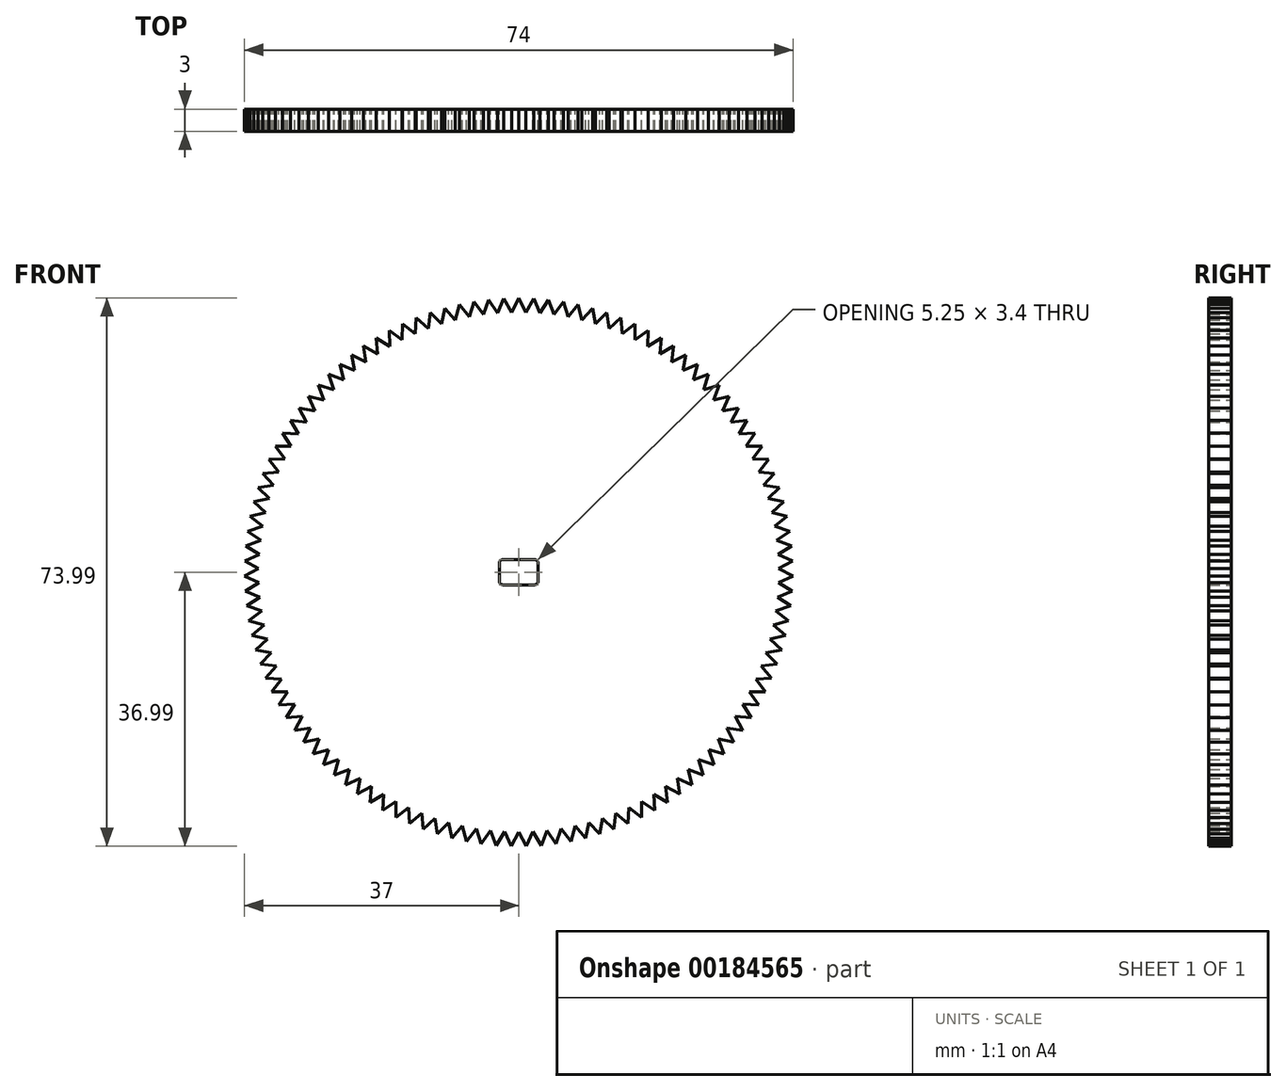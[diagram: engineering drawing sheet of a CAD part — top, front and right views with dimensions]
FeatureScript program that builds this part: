
annotation { "Feature Type Name" : "Feature", "Feature Type Description" : "" }
export const myFeature = defineFeature(function(context is Context, id is Id, definition is map)
    precondition{}
    {
        {
            var Q0;
            Q0=qCreatedBy(makeId("Front.planeOp"),FACE);
            var sketch = newSketch(context, id + "F0", { "sketchPlane" : qUnion([Q0])});
            skCircle(sketch, "E0", {"center": v(0, 0) * mm, "radius": 30 * mm});
            skSolve(sketch);
        }
        {
            var Q0;
            Q0=makeQuery(id+"F0.imprint","IMPRINT",FACE,{"disambiguationData":[TD([[makeQuery(id+"F0.imprint","IMPRINT",EDGE,{"derivedFrom":sQuery(id+"F0.wireOp",EDGE,"E0")}),1.0]])]});
            extrude(context, id + "F1", {"entities" : qUnion([Q0]), "depth" : 3 * mm});
        }
        {
            var Q0;
            Q0=makeQuery(id+"F1.opExtrude","CAP_FACE",FACE,{"disambiguationData":[OSD([sQuery(id+"F0.wireOp",EDGE,"E0")])],"isStart":false});
            var sketch = newSketch(context, id + "F2", { "sketchPlane" : qUnion([Q0])});
            skCircle(sketch, "E1", {"center": v(0, 0) * mm, "radius": 35 * mm});
            skLineSegment(sketch, "E2", {"start": v(-1, 34.99) * mm, "end": v(0, 37) * mm});
            skLineSegment(sketch, "E3", {"start": v(0, 37) * mm, "end": v(1, 34.99) * mm});
            skLineSegment(sketch, "E4.1.0", {"start": v(-2.02, 36.94) * mm, "end": v(-0.91, 34.99) * mm});
            skLineSegment(sketch, "E4.1.1", {"start": v(-2.9, 34.88) * mm, "end": v(-2.02, 36.94) * mm});
            skLineSegment(sketch, "E4.2.0", {"start": v(-4.04, 36.78) * mm, "end": v(-2.82, 34.89) * mm});
            skLineSegment(sketch, "E4.2.1", {"start": v(-4.8, 34.67) * mm, "end": v(-4.04, 36.78) * mm});
            skLineSegment(sketch, "E4.3.0", {"start": v(-6.04, 36.5) * mm, "end": v(-4.72, 34.68) * mm});
            skLineSegment(sketch, "E4.3.1", {"start": v(-6.7, 34.35) * mm, "end": v(-6.04, 36.5) * mm});
            skLineSegment(sketch, "E4.4.0", {"start": v(-8.02, 36.12) * mm, "end": v(-6.6, 34.37) * mm});
            skLineSegment(sketch, "E4.4.1", {"start": v(-8.56, 33.94) * mm, "end": v(-8.02, 36.12) * mm});
            skLineSegment(sketch, "E4.5.0", {"start": v(-9.98, 35.63) * mm, "end": v(-8.48, 33.96) * mm});
            skLineSegment(sketch, "E4.5.1", {"start": v(-10.4, 33.42) * mm, "end": v(-9.98, 35.63) * mm});
            skLineSegment(sketch, "E4.6.0", {"start": v(-11.91, 35.03) * mm, "end": v(-10.32, 33.44) * mm});
            skLineSegment(sketch, "E4.6.1", {"start": v(-12.21, 32.8) * mm, "end": v(-11.91, 35.03) * mm});
            skLineSegment(sketch, "E4.7.0", {"start": v(-13.8, 34.33) * mm, "end": v(-12.13, 32.83) * mm});
            skLineSegment(sketch, "E4.7.1", {"start": v(-13.98, 32.08) * mm, "end": v(-13.8, 34.33) * mm});
            skLineSegment(sketch, "E4.8.0", {"start": v(-15.66, 33.52) * mm, "end": v(-13.9, 32.12) * mm});
            skLineSegment(sketch, "E4.8.1", {"start": v(-15.72, 31.27) * mm, "end": v(-15.66, 33.52) * mm});
            skLineSegment(sketch, "E4.9.0", {"start": v(-17.47, 32.62) * mm, "end": v(-15.64, 31.31) * mm});
            skLineSegment(sketch, "E4.9.1", {"start": v(-17.4, 30.37) * mm, "end": v(-17.47, 32.62) * mm});
            skLineSegment(sketch, "E4.10.0", {"start": v(-19.22, 31.61) * mm, "end": v(-17.32, 30.41) * mm});
            skLineSegment(sketch, "E4.10.1", {"start": v(-19.03, 29.37) * mm, "end": v(-19.22, 31.61) * mm});
            skLineSegment(sketch, "E4.11.0", {"start": v(-20.92, 30.52) * mm, "end": v(-18.96, 29.42) * mm});
            skLineSegment(sketch, "E4.11.1", {"start": v(-20.6, 28.29) * mm, "end": v(-20.92, 30.52) * mm});
            skLineSegment(sketch, "E4.12.0", {"start": v(-22.56, 29.33) * mm, "end": v(-20.54, 28.34) * mm});
            skLineSegment(sketch, "E4.12.1", {"start": v(-22.12, 27.12) * mm, "end": v(-22.56, 29.33) * mm});
            skLineSegment(sketch, "E4.13.0", {"start": v(-24.13, 28.05) * mm, "end": v(-22.05, 27.18) * mm});
            skLineSegment(sketch, "E4.13.1", {"start": v(-23.57, 25.87) * mm, "end": v(-24.13, 28.05) * mm});
            skLineSegment(sketch, "E4.14.0", {"start": v(-25.62, 26.7) * mm, "end": v(-23.5, 25.93) * mm});
            skLineSegment(sketch, "E4.14.1", {"start": v(-24.95, 24.55) * mm, "end": v(-25.62, 26.7) * mm});
            skLineSegment(sketch, "E4.15.0", {"start": v(-27.04, 25.25) * mm, "end": v(-24.89, 24.61) * mm});
            skLineSegment(sketch, "E4.15.1", {"start": v(-26.25, 23.15) * mm, "end": v(-27.04, 25.25) * mm});
            skLineSegment(sketch, "E4.16.0", {"start": v(-28.38, 23.74) * mm, "end": v(-26.2, 23.21) * mm});
            skLineSegment(sketch, "E4.16.1", {"start": v(-27.48, 21.68) * mm, "end": v(-28.38, 23.74) * mm});
            skLineSegment(sketch, "E4.17.0", {"start": v(-29.63, 22.15) * mm, "end": v(-27.42, 21.75) * mm});
            skLineSegment(sketch, "E4.17.1", {"start": v(-28.62, 20.15) * mm, "end": v(-29.63, 22.15) * mm});
            skLineSegment(sketch, "E4.18.0", {"start": v(-30.8, 20.5) * mm, "end": v(-28.57, 20.22) * mm});
            skLineSegment(sketch, "E4.18.1", {"start": v(-29.68, 18.55) * mm, "end": v(-30.8, 20.5) * mm});
            skLineSegment(sketch, "E4.19.0", {"start": v(-31.87, 18.8) * mm, "end": v(-29.63, 18.63) * mm});
            skLineSegment(sketch, "E4.19.1", {"start": v(-30.65, 16.9) * mm, "end": v(-31.87, 18.8) * mm});
            skLineSegment(sketch, "E4.20.0", {"start": v(-32.85, 17.02) * mm, "end": v(-30.6, 16.98) * mm});
            skLineSegment(sketch, "E4.20.1", {"start": v(-31.52, 15.2) * mm, "end": v(-32.85, 17.02) * mm});
            skLineSegment(sketch, "E4.21.0", {"start": v(-33.73, 15.2) * mm, "end": v(-31.49, 15.29) * mm});
            skLineSegment(sketch, "E4.21.1", {"start": v(-32.3, 13.46) * mm, "end": v(-33.73, 15.2) * mm});
            skLineSegment(sketch, "E4.22.0", {"start": v(-34.51, 13.34) * mm, "end": v(-32.27, 13.54) * mm});
            skLineSegment(sketch, "E4.22.1", {"start": v(-33, 11.68) * mm, "end": v(-34.51, 13.34) * mm});
            skLineSegment(sketch, "E4.23.0", {"start": v(-35.19, 11.43) * mm, "end": v(-32.96, 11.76) * mm});
            skLineSegment(sketch, "E4.23.1", {"start": v(-33.58, 9.86) * mm, "end": v(-35.19, 11.43) * mm});
            skLineSegment(sketch, "E4.24.0", {"start": v(-35.76, 9.5) * mm, "end": v(-33.56, 9.94) * mm});
            skLineSegment(sketch, "E4.24.1", {"start": v(-34.07, 8.01) * mm, "end": v(-35.76, 9.5) * mm});
            skLineSegment(sketch, "E4.25.0", {"start": v(-36.23, 7.53) * mm, "end": v(-34.05, 8.1) * mm});
            skLineSegment(sketch, "E4.25.1", {"start": v(-34.46, 6.14) * mm, "end": v(-36.23, 7.53) * mm});
            skLineSegment(sketch, "E4.26.0", {"start": v(-36.58, 5.54) * mm, "end": v(-34.44, 6.23) * mm});
            skLineSegment(sketch, "E4.26.1", {"start": v(-34.74, 4.25) * mm, "end": v(-36.58, 5.54) * mm});
            skLineSegment(sketch, "E4.27.0", {"start": v(-36.83, 3.53) * mm, "end": v(-34.73, 4.34) * mm});
            skLineSegment(sketch, "E4.27.1", {"start": v(-34.92, 2.34) * mm, "end": v(-36.83, 3.53) * mm});
            skLineSegment(sketch, "E4.28.0", {"start": v(-36.97, 1.52) * mm, "end": v(-34.92, 2.43) * mm});
            skLineSegment(sketch, "E4.28.1", {"start": v(-35, 0.43) * mm, "end": v(-36.97, 1.52) * mm});
            skLineSegment(sketch, "E4.29.0", {"start": v(-37, -0.5) * mm, "end": v(-35, 0.52) * mm});
            skLineSegment(sketch, "E4.29.1", {"start": v(-34.97, -1.48) * mm, "end": v(-37, -0.5) * mm});
            skLineSegment(sketch, "E4.30.0", {"start": v(-36.91, -2.52) * mm, "end": v(-34.97, -1.39) * mm});
            skLineSegment(sketch, "E4.30.1", {"start": v(-34.84, -3.39) * mm, "end": v(-36.91, -2.52) * mm});
            skLineSegment(sketch, "E4.31.0", {"start": v(-36.72, -4.54) * mm, "end": v(-34.84, -3.3) * mm});
            skLineSegment(sketch, "E4.31.1", {"start": v(-34.6, -5.28) * mm, "end": v(-36.72, -4.54) * mm});
            skLineSegment(sketch, "E4.32.0", {"start": v(-36.42, -6.54) * mm, "end": v(-34.61, -5.2) * mm});
            skLineSegment(sketch, "E4.32.1", {"start": v(-34.26, -7.16) * mm, "end": v(-36.42, -6.54) * mm});
            skLineSegment(sketch, "E4.33.0", {"start": v(-36, -8.51) * mm, "end": v(-34.28, -7.08) * mm});
            skLineSegment(sketch, "E4.33.1", {"start": v(-33.82, -9.02) * mm, "end": v(-36, -8.51) * mm});
            skLineSegment(sketch, "E4.34.0", {"start": v(-35.49, -10.47) * mm, "end": v(-33.84, -8.94) * mm});
            skLineSegment(sketch, "E4.34.1", {"start": v(-33.27, -10.86) * mm, "end": v(-35.49, -10.47) * mm});
            skLineSegment(sketch, "E4.35.0", {"start": v(-34.86, -12.4) * mm, "end": v(-33.3, -10.77) * mm});
            skLineSegment(sketch, "E4.35.1", {"start": v(-32.63, -12.66) * mm, "end": v(-34.86, -12.4) * mm});
            skLineSegment(sketch, "E4.36.0", {"start": v(-34.13, -14.28) * mm, "end": v(-32.66, -12.58) * mm});
            skLineSegment(sketch, "E4.36.1", {"start": v(-31.9, -14.42) * mm, "end": v(-34.13, -14.28) * mm});
            skLineSegment(sketch, "E4.37.0", {"start": v(-33.3, -16.12) * mm, "end": v(-31.93, -14.34) * mm});
            skLineSegment(sketch, "E4.37.1", {"start": v(-31.06, -16.14) * mm, "end": v(-33.3, -16.12) * mm});
            skLineSegment(sketch, "E4.38.0", {"start": v(-32.37, -17.91) * mm, "end": v(-31.1, -16.06) * mm});
            skLineSegment(sketch, "E4.38.1", {"start": v(-30.13, -17.81) * mm, "end": v(-32.37, -17.91) * mm});
            skLineSegment(sketch, "E4.39.0", {"start": v(-31.35, -19.65) * mm, "end": v(-30.17, -17.74) * mm});
            skLineSegment(sketch, "E4.39.1", {"start": v(-29.11, -19.43) * mm, "end": v(-31.35, -19.65) * mm});
            skLineSegment(sketch, "E4.40.0", {"start": v(-30.23, -21.34) * mm, "end": v(-29.16, -19.36) * mm});
            skLineSegment(sketch, "E4.40.1", {"start": v(-28, -21) * mm, "end": v(-30.23, -21.34) * mm});
            skLineSegment(sketch, "E4.41.0", {"start": v(-29.02, -22.96) * mm, "end": v(-28.06, -20.92) * mm});
            skLineSegment(sketch, "E4.41.1", {"start": v(-26.82, -22.5) * mm, "end": v(-29.02, -22.96) * mm});
            skLineSegment(sketch, "E4.42.0", {"start": v(-27.72, -24.5) * mm, "end": v(-26.87, -22.42) * mm});
            skLineSegment(sketch, "E4.42.1", {"start": v(-25.55, -23.92) * mm, "end": v(-27.72, -24.5) * mm});
            skLineSegment(sketch, "E4.43.0", {"start": v(-26.34, -25.98) * mm, "end": v(-25.6, -23.86) * mm});
            skLineSegment(sketch, "E4.43.1", {"start": v(-24.2, -25.28) * mm, "end": v(-26.34, -25.98) * mm});
            skLineSegment(sketch, "E4.44.0", {"start": v(-24.88, -27.38) * mm, "end": v(-24.27, -25.22) * mm});
            skLineSegment(sketch, "E4.44.1", {"start": v(-22.79, -26.57) * mm, "end": v(-24.88, -27.38) * mm});
            skLineSegment(sketch, "E4.45.0", {"start": v(-23.35, -28.7) * mm, "end": v(-22.85, -26.5) * mm});
            skLineSegment(sketch, "E4.45.1", {"start": v(-21.3, -27.77) * mm, "end": v(-23.35, -28.7) * mm});
            skLineSegment(sketch, "E4.46.0", {"start": v(-21.75, -29.93) * mm, "end": v(-21.37, -27.72) * mm});
            skLineSegment(sketch, "E4.46.1", {"start": v(-19.76, -28.9) * mm, "end": v(-21.75, -29.93) * mm});
            skLineSegment(sketch, "E4.47.0", {"start": v(-20.08, -31.08) * mm, "end": v(-19.83, -28.84) * mm});
            skLineSegment(sketch, "E4.47.1", {"start": v(-18.15, -29.93) * mm, "end": v(-20.08, -31.08) * mm});
            skLineSegment(sketch, "E4.48.0", {"start": v(-18.35, -32.13) * mm, "end": v(-18.22, -29.88) * mm});
            skLineSegment(sketch, "E4.48.1", {"start": v(-16.49, -30.87) * mm, "end": v(-18.35, -32.13) * mm});
            skLineSegment(sketch, "E4.49.0", {"start": v(-16.57, -33.08) * mm, "end": v(-16.56, -30.83) * mm});
            skLineSegment(sketch, "E4.49.1", {"start": v(-14.78, -31.73) * mm, "end": v(-16.57, -33.08) * mm});
            skLineSegment(sketch, "E4.50.0", {"start": v(-14.74, -33.94) * mm, "end": v(-14.86, -31.7) * mm});
            skLineSegment(sketch, "E4.50.1", {"start": v(-13.02, -32.49) * mm, "end": v(-14.74, -33.94) * mm});
            skLineSegment(sketch, "E4.51.0", {"start": v(-12.87, -34.7) * mm, "end": v(-13.1, -32.45) * mm});
            skLineSegment(sketch, "E4.51.1", {"start": v(-11.23, -33.15) * mm, "end": v(-12.87, -34.7) * mm});
            skLineSegment(sketch, "E4.52.0", {"start": v(-10.95, -35.34) * mm, "end": v(-11.31, -33.12) * mm});
            skLineSegment(sketch, "E4.52.1", {"start": v(-9.4, -33.71) * mm, "end": v(-10.95, -35.34) * mm});
            skLineSegment(sketch, "E4.53.0", {"start": v(-9, -35.89) * mm, "end": v(-9.49, -33.7) * mm});
            skLineSegment(sketch, "E4.53.1", {"start": v(-7.55, -34.18) * mm, "end": v(-9, -35.89) * mm});
            skLineSegment(sketch, "E4.54.0", {"start": v(-7.03, -36.33) * mm, "end": v(-7.63, -34.16) * mm});
            skLineSegment(sketch, "E4.54.1", {"start": v(-5.67, -34.54) * mm, "end": v(-7.03, -36.33) * mm});
            skLineSegment(sketch, "E4.55.0", {"start": v(-5.04, -36.66) * mm, "end": v(-5.75, -34.52) * mm});
            skLineSegment(sketch, "E4.55.1", {"start": v(-3.77, -34.8) * mm, "end": v(-5.04, -36.66) * mm});
            skLineSegment(sketch, "E4.56.0", {"start": v(-3.03, -36.88) * mm, "end": v(-3.86, -34.79) * mm});
            skLineSegment(sketch, "E4.56.1", {"start": v(-1.87, -34.95) * mm, "end": v(-3.03, -36.88) * mm});
            skLineSegment(sketch, "E4.57.0", {"start": v(-1.01, -36.99) * mm, "end": v(-1.96, -34.95) * mm});
            skLineSegment(sketch, "E4.57.1", {"start": v(0.04, -35) * mm, "end": v(-1.01, -36.99) * mm});
            skLineSegment(sketch, "E4.58.0", {"start": v(1.01, -36.99) * mm, "end": v(-0.04, -35) * mm});
            skLineSegment(sketch, "E4.58.1", {"start": v(1.96, -34.95) * mm, "end": v(1.01, -36.99) * mm});
            skLineSegment(sketch, "E4.59.0", {"start": v(3.03, -36.88) * mm, "end": v(1.87, -34.95) * mm});
            skLineSegment(sketch, "E4.59.1", {"start": v(3.86, -34.79) * mm, "end": v(3.03, -36.88) * mm});
            skLineSegment(sketch, "E4.60.0", {"start": v(5.04, -36.66) * mm, "end": v(3.77, -34.8) * mm});
            skLineSegment(sketch, "E4.60.1", {"start": v(5.75, -34.52) * mm, "end": v(5.04, -36.66) * mm});
            skLineSegment(sketch, "E4.61.0", {"start": v(7.03, -36.33) * mm, "end": v(5.67, -34.54) * mm});
            skLineSegment(sketch, "E4.61.1", {"start": v(7.63, -34.16) * mm, "end": v(7.03, -36.33) * mm});
            skLineSegment(sketch, "E4.62.0", {"start": v(9, -35.89) * mm, "end": v(7.55, -34.18) * mm});
            skLineSegment(sketch, "E4.62.1", {"start": v(9.49, -33.7) * mm, "end": v(9, -35.89) * mm});
            skLineSegment(sketch, "E4.63.0", {"start": v(10.95, -35.34) * mm, "end": v(9.4, -33.71) * mm});
            skLineSegment(sketch, "E4.63.1", {"start": v(11.31, -33.12) * mm, "end": v(10.95, -35.34) * mm});
            skLineSegment(sketch, "E4.64.0", {"start": v(12.87, -34.7) * mm, "end": v(11.23, -33.15) * mm});
            skLineSegment(sketch, "E4.64.1", {"start": v(13.1, -32.45) * mm, "end": v(12.87, -34.7) * mm});
            skLineSegment(sketch, "E4.65.0", {"start": v(14.74, -33.94) * mm, "end": v(13.02, -32.49) * mm});
            skLineSegment(sketch, "E4.65.1", {"start": v(14.86, -31.7) * mm, "end": v(14.74, -33.94) * mm});
            skLineSegment(sketch, "E4.66.0", {"start": v(16.57, -33.08) * mm, "end": v(14.78, -31.73) * mm});
            skLineSegment(sketch, "E4.66.1", {"start": v(16.56, -30.83) * mm, "end": v(16.57, -33.08) * mm});
            skLineSegment(sketch, "E4.67.0", {"start": v(18.35, -32.13) * mm, "end": v(16.49, -30.87) * mm});
            skLineSegment(sketch, "E4.67.1", {"start": v(18.22, -29.88) * mm, "end": v(18.35, -32.13) * mm});
            skLineSegment(sketch, "E4.68.0", {"start": v(20.08, -31.08) * mm, "end": v(18.15, -29.93) * mm});
            skLineSegment(sketch, "E4.68.1", {"start": v(19.83, -28.84) * mm, "end": v(20.08, -31.08) * mm});
            skLineSegment(sketch, "E4.69.0", {"start": v(21.75, -29.93) * mm, "end": v(19.76, -28.9) * mm});
            skLineSegment(sketch, "E4.69.1", {"start": v(21.37, -27.72) * mm, "end": v(21.75, -29.93) * mm});
            skLineSegment(sketch, "E4.70.0", {"start": v(23.35, -28.7) * mm, "end": v(21.3, -27.77) * mm});
            skLineSegment(sketch, "E4.70.1", {"start": v(22.85, -26.5) * mm, "end": v(23.35, -28.7) * mm});
            skLineSegment(sketch, "E4.71.0", {"start": v(24.88, -27.38) * mm, "end": v(22.79, -26.57) * mm});
            skLineSegment(sketch, "E4.71.1", {"start": v(24.27, -25.22) * mm, "end": v(24.88, -27.38) * mm});
            skLineSegment(sketch, "E4.72.0", {"start": v(26.34, -25.98) * mm, "end": v(24.2, -25.28) * mm});
            skLineSegment(sketch, "E4.72.1", {"start": v(25.6, -23.86) * mm, "end": v(26.34, -25.98) * mm});
            skLineSegment(sketch, "E4.73.0", {"start": v(27.72, -24.5) * mm, "end": v(25.55, -23.92) * mm});
            skLineSegment(sketch, "E4.73.1", {"start": v(26.87, -22.42) * mm, "end": v(27.72, -24.5) * mm});
            skLineSegment(sketch, "E4.74.0", {"start": v(29.02, -22.96) * mm, "end": v(26.82, -22.5) * mm});
            skLineSegment(sketch, "E4.74.1", {"start": v(28.06, -20.92) * mm, "end": v(29.02, -22.96) * mm});
            skLineSegment(sketch, "E4.75.0", {"start": v(30.23, -21.34) * mm, "end": v(28, -21) * mm});
            skLineSegment(sketch, "E4.75.1", {"start": v(29.16, -19.36) * mm, "end": v(30.23, -21.34) * mm});
            skLineSegment(sketch, "E4.76.0", {"start": v(31.35, -19.65) * mm, "end": v(29.11, -19.43) * mm});
            skLineSegment(sketch, "E4.76.1", {"start": v(30.17, -17.74) * mm, "end": v(31.35, -19.65) * mm});
            skLineSegment(sketch, "E4.77.0", {"start": v(32.37, -17.91) * mm, "end": v(30.13, -17.81) * mm});
            skLineSegment(sketch, "E4.77.1", {"start": v(31.1, -16.06) * mm, "end": v(32.37, -17.91) * mm});
            skLineSegment(sketch, "E4.78.0", {"start": v(33.3, -16.12) * mm, "end": v(31.06, -16.14) * mm});
            skLineSegment(sketch, "E4.78.1", {"start": v(31.93, -14.34) * mm, "end": v(33.3, -16.12) * mm});
            skLineSegment(sketch, "E4.79.0", {"start": v(34.13, -14.28) * mm, "end": v(31.9, -14.42) * mm});
            skLineSegment(sketch, "E4.79.1", {"start": v(32.66, -12.58) * mm, "end": v(34.13, -14.28) * mm});
            skLineSegment(sketch, "E4.80.0", {"start": v(34.86, -12.4) * mm, "end": v(32.63, -12.66) * mm});
            skLineSegment(sketch, "E4.80.1", {"start": v(33.3, -10.77) * mm, "end": v(34.86, -12.4) * mm});
            skLineSegment(sketch, "E4.81.0", {"start": v(35.49, -10.47) * mm, "end": v(33.27, -10.86) * mm});
            skLineSegment(sketch, "E4.81.1", {"start": v(33.84, -8.94) * mm, "end": v(35.49, -10.47) * mm});
            skLineSegment(sketch, "E4.82.0", {"start": v(36, -8.51) * mm, "end": v(33.82, -9.02) * mm});
            skLineSegment(sketch, "E4.82.1", {"start": v(34.28, -7.08) * mm, "end": v(36, -8.51) * mm});
            skLineSegment(sketch, "E4.83.0", {"start": v(36.42, -6.54) * mm, "end": v(34.26, -7.16) * mm});
            skLineSegment(sketch, "E4.83.1", {"start": v(34.61, -5.2) * mm, "end": v(36.42, -6.54) * mm});
            skLineSegment(sketch, "E4.84.0", {"start": v(36.72, -4.54) * mm, "end": v(34.6, -5.28) * mm});
            skLineSegment(sketch, "E4.84.1", {"start": v(34.84, -3.3) * mm, "end": v(36.72, -4.54) * mm});
            skLineSegment(sketch, "E5.2.85.0", {"start": v(36.91, -2.52) * mm, "end": v(34.84, -3.39) * mm});
            skLineSegment(sketch, "E5.3.85.0", {"start": v(34.97, -1.39) * mm, "end": v(36.91, -2.52) * mm});
            skLineSegment(sketch, "E5.2.86.0", {"start": v(37, -0.5) * mm, "end": v(34.97, -1.48) * mm});
            skLineSegment(sketch, "E5.3.86.0", {"start": v(35, 0.52) * mm, "end": v(37, -0.5) * mm});
            skLineSegment(sketch, "E5.2.87.0", {"start": v(36.97, 1.52) * mm, "end": v(35, 0.43) * mm});
            skLineSegment(sketch, "E5.3.87.0", {"start": v(34.92, 2.43) * mm, "end": v(36.97, 1.52) * mm});
            skLineSegment(sketch, "E5.2.88.0", {"start": v(36.83, 3.53) * mm, "end": v(34.92, 2.34) * mm});
            skLineSegment(sketch, "E5.3.88.0", {"start": v(34.73, 4.34) * mm, "end": v(36.83, 3.53) * mm});
            skLineSegment(sketch, "E5.2.89.0", {"start": v(36.58, 5.54) * mm, "end": v(34.74, 4.25) * mm});
            skLineSegment(sketch, "E5.3.89.0", {"start": v(34.44, 6.23) * mm, "end": v(36.58, 5.54) * mm});
            skLineSegment(sketch, "E5.2.90.0", {"start": v(36.23, 7.53) * mm, "end": v(34.46, 6.14) * mm});
            skLineSegment(sketch, "E5.3.90.0", {"start": v(34.05, 8.1) * mm, "end": v(36.23, 7.53) * mm});
            skLineSegment(sketch, "E5.2.91.0", {"start": v(35.76, 9.5) * mm, "end": v(34.07, 8.01) * mm});
            skLineSegment(sketch, "E5.3.91.0", {"start": v(33.56, 9.94) * mm, "end": v(35.76, 9.5) * mm});
            skLineSegment(sketch, "E5.2.92.0", {"start": v(35.19, 11.43) * mm, "end": v(33.58, 9.86) * mm});
            skLineSegment(sketch, "E5.3.92.0", {"start": v(32.96, 11.76) * mm, "end": v(35.19, 11.43) * mm});
            skLineSegment(sketch, "E5.2.93.0", {"start": v(34.51, 13.34) * mm, "end": v(33, 11.68) * mm});
            skLineSegment(sketch, "E5.3.93.0", {"start": v(32.27, 13.54) * mm, "end": v(34.51, 13.34) * mm});
            skLineSegment(sketch, "E5.2.94.0", {"start": v(33.73, 15.2) * mm, "end": v(32.3, 13.46) * mm});
            skLineSegment(sketch, "E5.3.94.0", {"start": v(31.49, 15.29) * mm, "end": v(33.73, 15.2) * mm});
            skLineSegment(sketch, "E5.2.95.0", {"start": v(32.85, 17.02) * mm, "end": v(31.52, 15.2) * mm});
            skLineSegment(sketch, "E5.3.95.0", {"start": v(30.6, 16.98) * mm, "end": v(32.85, 17.02) * mm});
            skLineSegment(sketch, "E5.2.96.0", {"start": v(31.87, 18.8) * mm, "end": v(30.65, 16.9) * mm});
            skLineSegment(sketch, "E5.3.96.0", {"start": v(29.63, 18.63) * mm, "end": v(31.87, 18.8) * mm});
            skLineSegment(sketch, "E5.2.97.0", {"start": v(30.8, 20.5) * mm, "end": v(29.68, 18.55) * mm});
            skLineSegment(sketch, "E5.3.97.0", {"start": v(28.57, 20.22) * mm, "end": v(30.8, 20.5) * mm});
            skLineSegment(sketch, "E5.2.98.0", {"start": v(29.63, 22.15) * mm, "end": v(28.62, 20.15) * mm});
            skLineSegment(sketch, "E5.3.98.0", {"start": v(27.42, 21.75) * mm, "end": v(29.63, 22.15) * mm});
            skLineSegment(sketch, "E5.2.99.0", {"start": v(28.38, 23.74) * mm, "end": v(27.48, 21.68) * mm});
            skLineSegment(sketch, "E5.3.99.0", {"start": v(26.2, 23.21) * mm, "end": v(28.38, 23.74) * mm});
            skLineSegment(sketch, "E6.2.100.0", {"start": v(27.04, 25.25) * mm, "end": v(26.25, 23.15) * mm});
            skLineSegment(sketch, "E6.3.100.0", {"start": v(24.89, 24.61) * mm, "end": v(27.04, 25.25) * mm});
            skLineSegment(sketch, "E6.2.101.0", {"start": v(25.62, 26.7) * mm, "end": v(24.95, 24.55) * mm});
            skLineSegment(sketch, "E6.3.101.0", {"start": v(23.5, 25.93) * mm, "end": v(25.62, 26.7) * mm});
            skLineSegment(sketch, "E6.2.102.0", {"start": v(24.13, 28.05) * mm, "end": v(23.57, 25.87) * mm});
            skLineSegment(sketch, "E6.3.102.0", {"start": v(22.05, 27.18) * mm, "end": v(24.13, 28.05) * mm});
            skLineSegment(sketch, "E6.2.103.0", {"start": v(22.56, 29.33) * mm, "end": v(22.12, 27.12) * mm});
            skLineSegment(sketch, "E6.3.103.0", {"start": v(20.54, 28.34) * mm, "end": v(22.56, 29.33) * mm});
            skLineSegment(sketch, "E6.2.104.0", {"start": v(20.92, 30.52) * mm, "end": v(20.6, 28.29) * mm});
            skLineSegment(sketch, "E6.3.104.0", {"start": v(18.96, 29.42) * mm, "end": v(20.92, 30.52) * mm});
            skLineSegment(sketch, "E6.2.105.0", {"start": v(19.22, 31.61) * mm, "end": v(19.03, 29.37) * mm});
            skLineSegment(sketch, "E6.3.105.0", {"start": v(17.32, 30.41) * mm, "end": v(19.22, 31.61) * mm});
            skLineSegment(sketch, "E6.2.106.0", {"start": v(17.47, 32.62) * mm, "end": v(17.4, 30.37) * mm});
            skLineSegment(sketch, "E6.3.106.0", {"start": v(15.64, 31.31) * mm, "end": v(17.47, 32.62) * mm});
            skLineSegment(sketch, "E6.2.107.0", {"start": v(15.66, 33.52) * mm, "end": v(15.72, 31.27) * mm});
            skLineSegment(sketch, "E6.3.107.0", {"start": v(13.9, 32.12) * mm, "end": v(15.66, 33.52) * mm});
            skLineSegment(sketch, "E6.2.108.0", {"start": v(13.8, 34.33) * mm, "end": v(13.98, 32.08) * mm});
            skLineSegment(sketch, "E6.3.108.0", {"start": v(12.13, 32.83) * mm, "end": v(13.8, 34.33) * mm});
            skLineSegment(sketch, "E6.2.109.0", {"start": v(11.91, 35.03) * mm, "end": v(12.21, 32.8) * mm});
            skLineSegment(sketch, "E6.3.109.0", {"start": v(10.32, 33.44) * mm, "end": v(11.91, 35.03) * mm});
            skLineSegment(sketch, "E6.2.110.0", {"start": v(9.98, 35.63) * mm, "end": v(10.4, 33.42) * mm});
            skLineSegment(sketch, "E6.3.110.0", {"start": v(8.48, 33.96) * mm, "end": v(9.98, 35.63) * mm});
            skLineSegment(sketch, "E6.2.111.0", {"start": v(8.02, 36.12) * mm, "end": v(8.56, 33.94) * mm});
            skLineSegment(sketch, "E6.3.111.0", {"start": v(6.6, 34.37) * mm, "end": v(8.02, 36.12) * mm});
            skLineSegment(sketch, "E6.2.112.0", {"start": v(6.04, 36.5) * mm, "end": v(6.7, 34.35) * mm});
            skLineSegment(sketch, "E6.3.112.0", {"start": v(4.72, 34.68) * mm, "end": v(6.04, 36.5) * mm});
            skLineSegment(sketch, "E6.2.113.0", {"start": v(4.04, 36.78) * mm, "end": v(4.8, 34.67) * mm});
            skLineSegment(sketch, "E6.3.113.0", {"start": v(2.82, 34.89) * mm, "end": v(4.04, 36.78) * mm});
            skLineSegment(sketch, "E6.2.114.0", {"start": v(2.02, 36.94) * mm, "end": v(2.9, 34.88) * mm});
            skLineSegment(sketch, "E6.3.114.0", {"start": v(0.91, 34.99) * mm, "end": v(2.02, 36.94) * mm});
            skSolve(sketch);
        }
        {
            var Q0;
            Q0=makeQuery(id+"F2.imprint","IMPRINT",FACE,{"disambiguationData":[TD([[makeQuery(id+"F2.imprint","IMPRINT",EDGE,{"derivedFrom":makeQuery(id+"F1.opExtrude","CAP_EDGE",EDGE,{"disambiguationData":[OSD([sQuery(id+"F0.wireOp",EDGE,"E0")])],"isStart":false})}),-1.0]])]});
            var Q1;
            {var subQ3=sQuery(id+"F2.wireOp",EDGE,"E4.8.1");var subQ5=sQuery(id+"F2.wireOp",EDGE,"E1");var subQ6=makeQuery(id+"F2.imprint","INTERSECT",VERTEX,{"derivedFrom":[subQ5,subQ3]});Q1=makeQuery(id+"F2.imprint","IMPRINT",FACE,{"disambiguationData":[TD([[makeQuery(id+"F2.imprint","IMPRINT",EDGE,{"disambiguationData":[TD([[subQ6,-1.0]])],"derivedFrom":subQ5}),-1.0]])]});}
            var Q2;
            {var subQ5=sQuery(id+"F2.wireOp",EDGE,"E4.7.1");var subQ7=sQuery(id+"F2.wireOp",EDGE,"E1");var subQ8=makeQuery(id+"F2.imprint","INTERSECT",VERTEX,{"derivedFrom":[subQ7,subQ5]});Q2=makeQuery(id+"F2.imprint","IMPRINT",FACE,{"disambiguationData":[TD([[makeQuery(id+"F2.imprint","IMPRINT",EDGE,{"disambiguationData":[TD([[subQ8,-1.0]])],"derivedFrom":subQ7}),-1.0]])]});}
            var Q3;
            {var subQ5=sQuery(id+"F2.wireOp",EDGE,"E4.6.1");var subQ7=sQuery(id+"F2.wireOp",EDGE,"E1");var subQ8=makeQuery(id+"F2.imprint","INTERSECT",VERTEX,{"derivedFrom":[subQ7,subQ5]});Q3=makeQuery(id+"F2.imprint","IMPRINT",FACE,{"disambiguationData":[TD([[makeQuery(id+"F2.imprint","IMPRINT",EDGE,{"disambiguationData":[TD([[subQ8,-1.0]])],"derivedFrom":subQ7}),-1.0]])]});}
            var Q4;
            {var subQ5=sQuery(id+"F2.wireOp",EDGE,"E4.5.1");var subQ6=sQuery(id+"F2.wireOp",EDGE,"E1");var subQ7=makeQuery(id+"F2.imprint","INTERSECT",VERTEX,{"derivedFrom":[subQ6,subQ5]});Q4=makeQuery(id+"F2.imprint","IMPRINT",FACE,{"disambiguationData":[TD([[makeQuery(id+"F2.imprint","IMPRINT",EDGE,{"disambiguationData":[TD([[subQ7,-1.0]])],"derivedFrom":subQ6}),-1.0]])]});}
            var Q5;
            {var subQ3=sQuery(id+"F2.wireOp",EDGE,"E4.4.1");var subQ5=sQuery(id+"F2.wireOp",EDGE,"E1");var subQ6=makeQuery(id+"F2.imprint","INTERSECT",VERTEX,{"derivedFrom":[subQ5,subQ3]});Q5=makeQuery(id+"F2.imprint","IMPRINT",FACE,{"disambiguationData":[TD([[makeQuery(id+"F2.imprint","IMPRINT",EDGE,{"disambiguationData":[TD([[subQ6,-1.0]])],"derivedFrom":subQ5}),-1.0]])]});}
            var Q6;
            {var subQ5=sQuery(id+"F2.wireOp",EDGE,"E4.3.1");var subQ7=sQuery(id+"F2.wireOp",EDGE,"E1");var subQ8=makeQuery(id+"F2.imprint","INTERSECT",VERTEX,{"derivedFrom":[subQ7,subQ5]});Q6=makeQuery(id+"F2.imprint","IMPRINT",FACE,{"disambiguationData":[TD([[makeQuery(id+"F2.imprint","IMPRINT",EDGE,{"disambiguationData":[TD([[subQ8,-1.0]])],"derivedFrom":subQ7}),-1.0]])]});}
            var Q7;
            {var subQ5=sQuery(id+"F2.wireOp",EDGE,"E4.2.1");var subQ7=sQuery(id+"F2.wireOp",EDGE,"E1");var subQ8=makeQuery(id+"F2.imprint","INTERSECT",VERTEX,{"derivedFrom":[subQ7,subQ5]});Q7=makeQuery(id+"F2.imprint","IMPRINT",FACE,{"disambiguationData":[TD([[makeQuery(id+"F2.imprint","IMPRINT",EDGE,{"disambiguationData":[TD([[subQ8,-1.0]])],"derivedFrom":subQ7}),-1.0]])]});}
            var Q8;
            {var subQ3=sQuery(id+"F2.wireOp",EDGE,"E4.1.1");var subQ7=sQuery(id+"F2.wireOp",EDGE,"E1");var subQ8=makeQuery(id+"F2.imprint","INTERSECT",VERTEX,{"derivedFrom":[subQ7,subQ3]});Q8=makeQuery(id+"F2.imprint","IMPRINT",FACE,{"disambiguationData":[TD([[makeQuery(id+"F2.imprint","IMPRINT",EDGE,{"disambiguationData":[TD([[subQ8,-1.0]])],"derivedFrom":subQ7}),-1.0]])]});}
            var Q9;
            {var subQ5=sQuery(id+"F2.wireOp",EDGE,"E2");var subQ7=sQuery(id+"F2.wireOp",EDGE,"E1");var subQ8=makeQuery(id+"F2.imprint","INTERSECT",VERTEX,{"derivedFrom":[subQ7,subQ5]});Q9=makeQuery(id+"F2.imprint","IMPRINT",FACE,{"disambiguationData":[TD([[makeQuery(id+"F2.imprint","IMPRINT",EDGE,{"disambiguationData":[TD([[subQ8,-1.0]])],"derivedFrom":subQ7}),-1.0]])]});}
            var Q10;
            {var subQ0=sQuery(id+"F2.wireOp",EDGE,"E4.1.0");var subQ1=sQuery(id+"F2.wireOp",EDGE,"E1");var subQ2=makeQuery(id+"F2.imprint","INTERSECT",VERTEX,{"derivedFrom":[subQ1,subQ0]});Q10=makeQuery(id+"F2.imprint","IMPRINT",FACE,{"disambiguationData":[TD([[makeQuery(id+"F2.imprint","IMPRINT",EDGE,{"disambiguationData":[TD([[subQ2,1.0]])],"derivedFrom":subQ1}),-1.0]])]});}
            var Q11;
            {var subQ5=sQuery(id+"F2.wireOp",EDGE,"E1");var subQ7=sQuery(id+"F2.wireOp",EDGE,"E3");var subQ8=makeQuery(id+"F2.imprint","INTERSECT",VERTEX,{"derivedFrom":[subQ5,subQ7]});Q11=makeQuery(id+"F2.imprint","IMPRINT",FACE,{"disambiguationData":[TD([[makeQuery(id+"F2.imprint","IMPRINT",EDGE,{"disambiguationData":[TD([[subQ8,1.0]])],"derivedFrom":subQ5}),-1.0]])]});}
            var Q12;
            {var subQ0=sQuery(id+"F2.wireOp",EDGE,"E5.3.86.0");var subQ1=sQuery(id+"F2.wireOp",EDGE,"E1");var subQ2=makeQuery(id+"F2.imprint","INTERSECT",VERTEX,{"derivedFrom":[subQ1,subQ0]});Q12=makeQuery(id+"F2.imprint","IMPRINT",FACE,{"disambiguationData":[TD([[makeQuery(id+"F2.imprint","IMPRINT",EDGE,{"disambiguationData":[TD([[subQ2,1.0]])],"derivedFrom":subQ1}),-1.0]])]});}
            var Q13;
            {var subQ0=sQuery(id+"F2.wireOp",EDGE,"E5.3.87.0");var subQ1=sQuery(id+"F2.wireOp",EDGE,"E1");var subQ2=makeQuery(id+"F2.imprint","INTERSECT",VERTEX,{"derivedFrom":[subQ1,subQ0]});Q13=makeQuery(id+"F2.imprint","IMPRINT",FACE,{"disambiguationData":[TD([[makeQuery(id+"F2.imprint","IMPRINT",EDGE,{"disambiguationData":[TD([[subQ2,1.0]])],"derivedFrom":subQ1}),-1.0]])]});}
            var Q14;
            {var subQ0=sQuery(id+"F2.wireOp",EDGE,"E5.3.88.0");var subQ1=sQuery(id+"F2.wireOp",EDGE,"E1");var subQ2=makeQuery(id+"F2.imprint","INTERSECT",VERTEX,{"derivedFrom":[subQ1,subQ0]});Q14=makeQuery(id+"F2.imprint","IMPRINT",FACE,{"disambiguationData":[TD([[makeQuery(id+"F2.imprint","IMPRINT",EDGE,{"disambiguationData":[TD([[subQ2,1.0]])],"derivedFrom":subQ1}),-1.0]])]});}
            var Q15;
            {var subQ0=sQuery(id+"F2.wireOp",EDGE,"E5.3.89.0");var subQ1=sQuery(id+"F2.wireOp",EDGE,"E1");var subQ2=makeQuery(id+"F2.imprint","INTERSECT",VERTEX,{"derivedFrom":[subQ1,subQ0]});Q15=makeQuery(id+"F2.imprint","IMPRINT",FACE,{"disambiguationData":[TD([[makeQuery(id+"F2.imprint","IMPRINT",EDGE,{"disambiguationData":[TD([[subQ2,1.0]])],"derivedFrom":subQ1}),-1.0]])]});}
            var Q16;
            {var subQ0=sQuery(id+"F2.wireOp",EDGE,"E5.3.90.0");var subQ1=sQuery(id+"F2.wireOp",EDGE,"E1");var subQ2=makeQuery(id+"F2.imprint","INTERSECT",VERTEX,{"derivedFrom":[subQ1,subQ0]});Q16=makeQuery(id+"F2.imprint","IMPRINT",FACE,{"disambiguationData":[TD([[makeQuery(id+"F2.imprint","IMPRINT",EDGE,{"disambiguationData":[TD([[subQ2,1.0]])],"derivedFrom":subQ1}),-1.0]])]});}
            var Q17;
            {var subQ0=sQuery(id+"F2.wireOp",EDGE,"E5.3.91.0");var subQ1=sQuery(id+"F2.wireOp",EDGE,"E1");var subQ2=makeQuery(id+"F2.imprint","INTERSECT",VERTEX,{"derivedFrom":[subQ1,subQ0]});Q17=makeQuery(id+"F2.imprint","IMPRINT",FACE,{"disambiguationData":[TD([[makeQuery(id+"F2.imprint","IMPRINT",EDGE,{"disambiguationData":[TD([[subQ2,1.0]])],"derivedFrom":subQ1}),-1.0]])]});}
            var Q18;
            {var subQ0=sQuery(id+"F2.wireOp",EDGE,"E5.3.92.0");var subQ1=sQuery(id+"F2.wireOp",EDGE,"E1");var subQ2=makeQuery(id+"F2.imprint","INTERSECT",VERTEX,{"derivedFrom":[subQ1,subQ0]});Q18=makeQuery(id+"F2.imprint","IMPRINT",FACE,{"disambiguationData":[TD([[makeQuery(id+"F2.imprint","IMPRINT",EDGE,{"disambiguationData":[TD([[subQ2,1.0]])],"derivedFrom":subQ1}),-1.0]])]});}
            var Q19;
            {var subQ0=sQuery(id+"F2.wireOp",EDGE,"E5.3.93.0");var subQ1=sQuery(id+"F2.wireOp",EDGE,"E1");var subQ2=makeQuery(id+"F2.imprint","INTERSECT",VERTEX,{"derivedFrom":[subQ1,subQ0]});Q19=makeQuery(id+"F2.imprint","IMPRINT",FACE,{"disambiguationData":[TD([[makeQuery(id+"F2.imprint","IMPRINT",EDGE,{"disambiguationData":[TD([[subQ2,1.0]])],"derivedFrom":subQ1}),-1.0]])]});}
            var Q20;
            {var subQ0=sQuery(id+"F2.wireOp",EDGE,"E5.3.94.0");var subQ1=sQuery(id+"F2.wireOp",EDGE,"E1");var subQ2=makeQuery(id+"F2.imprint","INTERSECT",VERTEX,{"derivedFrom":[subQ1,subQ0]});Q20=makeQuery(id+"F2.imprint","IMPRINT",FACE,{"disambiguationData":[TD([[makeQuery(id+"F2.imprint","IMPRINT",EDGE,{"disambiguationData":[TD([[subQ2,1.0]])],"derivedFrom":subQ1}),-1.0]])]});}
            var Q21;
            {var subQ0=sQuery(id+"F2.wireOp",EDGE,"E5.3.95.0");var subQ1=sQuery(id+"F2.wireOp",EDGE,"E1");var subQ2=makeQuery(id+"F2.imprint","INTERSECT",VERTEX,{"derivedFrom":[subQ1,subQ0]});Q21=makeQuery(id+"F2.imprint","IMPRINT",FACE,{"disambiguationData":[TD([[makeQuery(id+"F2.imprint","IMPRINT",EDGE,{"disambiguationData":[TD([[subQ2,1.0]])],"derivedFrom":subQ1}),-1.0]])]});}
            var Q22;
            {var subQ0=sQuery(id+"F2.wireOp",EDGE,"E5.3.96.0");var subQ1=sQuery(id+"F2.wireOp",EDGE,"E1");var subQ2=makeQuery(id+"F2.imprint","INTERSECT",VERTEX,{"derivedFrom":[subQ1,subQ0]});Q22=makeQuery(id+"F2.imprint","IMPRINT",FACE,{"disambiguationData":[TD([[makeQuery(id+"F2.imprint","IMPRINT",EDGE,{"disambiguationData":[TD([[subQ2,1.0]])],"derivedFrom":subQ1}),-1.0]])]});}
            var Q23;
            {var subQ0=sQuery(id+"F2.wireOp",EDGE,"E5.3.97.0");var subQ1=sQuery(id+"F2.wireOp",EDGE,"E1");var subQ2=makeQuery(id+"F2.imprint","INTERSECT",VERTEX,{"derivedFrom":[subQ1,subQ0]});Q23=makeQuery(id+"F2.imprint","IMPRINT",FACE,{"disambiguationData":[TD([[makeQuery(id+"F2.imprint","IMPRINT",EDGE,{"disambiguationData":[TD([[subQ2,1.0]])],"derivedFrom":subQ1}),-1.0]])]});}
            var Q24;
            {var subQ0=sQuery(id+"F2.wireOp",EDGE,"E5.3.98.0");var subQ1=sQuery(id+"F2.wireOp",EDGE,"E1");var subQ2=makeQuery(id+"F2.imprint","INTERSECT",VERTEX,{"derivedFrom":[subQ1,subQ0]});Q24=makeQuery(id+"F2.imprint","IMPRINT",FACE,{"disambiguationData":[TD([[makeQuery(id+"F2.imprint","IMPRINT",EDGE,{"disambiguationData":[TD([[subQ2,1.0]])],"derivedFrom":subQ1}),-1.0]])]});}
            var Q25;
            {var subQ0=sQuery(id+"F2.wireOp",EDGE,"E5.3.99.0");var subQ1=sQuery(id+"F2.wireOp",EDGE,"E1");var subQ2=makeQuery(id+"F2.imprint","INTERSECT",VERTEX,{"derivedFrom":[subQ1,subQ0]});Q25=makeQuery(id+"F2.imprint","IMPRINT",FACE,{"disambiguationData":[TD([[makeQuery(id+"F2.imprint","IMPRINT",EDGE,{"disambiguationData":[TD([[subQ2,1.0]])],"derivedFrom":subQ1}),-1.0]])]});}
            var Q26;
            {var subQ0=sQuery(id+"F2.wireOp",EDGE,"E6.3.100.0");var subQ1=sQuery(id+"F2.wireOp",EDGE,"E1");var subQ2=makeQuery(id+"F2.imprint","INTERSECT",VERTEX,{"derivedFrom":[subQ1,subQ0]});Q26=makeQuery(id+"F2.imprint","IMPRINT",FACE,{"disambiguationData":[TD([[makeQuery(id+"F2.imprint","IMPRINT",EDGE,{"disambiguationData":[TD([[subQ2,1.0]])],"derivedFrom":subQ1}),-1.0]])]});}
            var Q27;
            {var subQ0=sQuery(id+"F2.wireOp",EDGE,"E6.3.101.0");var subQ1=sQuery(id+"F2.wireOp",EDGE,"E1");var subQ2=makeQuery(id+"F2.imprint","INTERSECT",VERTEX,{"derivedFrom":[subQ1,subQ0]});Q27=makeQuery(id+"F2.imprint","IMPRINT",FACE,{"disambiguationData":[TD([[makeQuery(id+"F2.imprint","IMPRINT",EDGE,{"disambiguationData":[TD([[subQ2,1.0]])],"derivedFrom":subQ1}),-1.0]])]});}
            var Q28;
            {var subQ0=sQuery(id+"F2.wireOp",EDGE,"E6.3.102.0");var subQ1=sQuery(id+"F2.wireOp",EDGE,"E1");var subQ2=makeQuery(id+"F2.imprint","INTERSECT",VERTEX,{"derivedFrom":[subQ1,subQ0]});Q28=makeQuery(id+"F2.imprint","IMPRINT",FACE,{"disambiguationData":[TD([[makeQuery(id+"F2.imprint","IMPRINT",EDGE,{"disambiguationData":[TD([[subQ2,1.0]])],"derivedFrom":subQ1}),-1.0]])]});}
            var Q29;
            {var subQ0=sQuery(id+"F2.wireOp",EDGE,"E6.3.103.0");var subQ1=sQuery(id+"F2.wireOp",EDGE,"E1");var subQ2=makeQuery(id+"F2.imprint","INTERSECT",VERTEX,{"derivedFrom":[subQ1,subQ0]});Q29=makeQuery(id+"F2.imprint","IMPRINT",FACE,{"disambiguationData":[TD([[makeQuery(id+"F2.imprint","IMPRINT",EDGE,{"disambiguationData":[TD([[subQ2,1.0]])],"derivedFrom":subQ1}),-1.0]])]});}
            var Q30;
            {var subQ0=sQuery(id+"F2.wireOp",EDGE,"E6.3.104.0");var subQ1=sQuery(id+"F2.wireOp",EDGE,"E1");var subQ2=makeQuery(id+"F2.imprint","INTERSECT",VERTEX,{"derivedFrom":[subQ1,subQ0]});Q30=makeQuery(id+"F2.imprint","IMPRINT",FACE,{"disambiguationData":[TD([[makeQuery(id+"F2.imprint","IMPRINT",EDGE,{"disambiguationData":[TD([[subQ2,1.0]])],"derivedFrom":subQ1}),-1.0]])]});}
            var Q31;
            {var subQ0=sQuery(id+"F2.wireOp",EDGE,"E6.3.105.0");var subQ1=sQuery(id+"F2.wireOp",EDGE,"E1");var subQ2=makeQuery(id+"F2.imprint","INTERSECT",VERTEX,{"derivedFrom":[subQ1,subQ0]});Q31=makeQuery(id+"F2.imprint","IMPRINT",FACE,{"disambiguationData":[TD([[makeQuery(id+"F2.imprint","IMPRINT",EDGE,{"disambiguationData":[TD([[subQ2,1.0]])],"derivedFrom":subQ1}),-1.0]])]});}
            var Q32;
            {var subQ0=sQuery(id+"F2.wireOp",EDGE,"E6.3.106.0");var subQ1=sQuery(id+"F2.wireOp",EDGE,"E1");var subQ2=makeQuery(id+"F2.imprint","INTERSECT",VERTEX,{"derivedFrom":[subQ1,subQ0]});Q32=makeQuery(id+"F2.imprint","IMPRINT",FACE,{"disambiguationData":[TD([[makeQuery(id+"F2.imprint","IMPRINT",EDGE,{"disambiguationData":[TD([[subQ2,1.0]])],"derivedFrom":subQ1}),-1.0]])]});}
            var Q33;
            {var subQ0=sQuery(id+"F2.wireOp",EDGE,"E6.3.107.0");var subQ1=sQuery(id+"F2.wireOp",EDGE,"E1");var subQ2=makeQuery(id+"F2.imprint","INTERSECT",VERTEX,{"derivedFrom":[subQ1,subQ0]});Q33=makeQuery(id+"F2.imprint","IMPRINT",FACE,{"disambiguationData":[TD([[makeQuery(id+"F2.imprint","IMPRINT",EDGE,{"disambiguationData":[TD([[subQ2,1.0]])],"derivedFrom":subQ1}),-1.0]])]});}
            var Q34;
            {var subQ0=sQuery(id+"F2.wireOp",EDGE,"E6.3.108.0");var subQ1=sQuery(id+"F2.wireOp",EDGE,"E1");var subQ2=makeQuery(id+"F2.imprint","INTERSECT",VERTEX,{"derivedFrom":[subQ1,subQ0]});Q34=makeQuery(id+"F2.imprint","IMPRINT",FACE,{"disambiguationData":[TD([[makeQuery(id+"F2.imprint","IMPRINT",EDGE,{"disambiguationData":[TD([[subQ2,1.0]])],"derivedFrom":subQ1}),-1.0]])]});}
            var Q35;
            {var subQ0=sQuery(id+"F2.wireOp",EDGE,"E6.3.109.0");var subQ1=sQuery(id+"F2.wireOp",EDGE,"E1");var subQ2=makeQuery(id+"F2.imprint","INTERSECT",VERTEX,{"derivedFrom":[subQ1,subQ0]});Q35=makeQuery(id+"F2.imprint","IMPRINT",FACE,{"disambiguationData":[TD([[makeQuery(id+"F2.imprint","IMPRINT",EDGE,{"disambiguationData":[TD([[subQ2,1.0]])],"derivedFrom":subQ1}),-1.0]])]});}
            var Q36;
            {var subQ0=sQuery(id+"F2.wireOp",EDGE,"E6.3.110.0");var subQ1=sQuery(id+"F2.wireOp",EDGE,"E1");var subQ2=makeQuery(id+"F2.imprint","INTERSECT",VERTEX,{"derivedFrom":[subQ1,subQ0]});Q36=makeQuery(id+"F2.imprint","IMPRINT",FACE,{"disambiguationData":[TD([[makeQuery(id+"F2.imprint","IMPRINT",EDGE,{"disambiguationData":[TD([[subQ2,1.0]])],"derivedFrom":subQ1}),-1.0]])]});}
            var Q37;
            {var subQ0=sQuery(id+"F2.wireOp",EDGE,"E6.3.111.0");var subQ1=sQuery(id+"F2.wireOp",EDGE,"E1");var subQ2=makeQuery(id+"F2.imprint","INTERSECT",VERTEX,{"derivedFrom":[subQ1,subQ0]});Q37=makeQuery(id+"F2.imprint","IMPRINT",FACE,{"disambiguationData":[TD([[makeQuery(id+"F2.imprint","IMPRINT",EDGE,{"disambiguationData":[TD([[subQ2,1.0]])],"derivedFrom":subQ1}),-1.0]])]});}
            var Q38;
            {var subQ0=sQuery(id+"F2.wireOp",EDGE,"E6.3.112.0");var subQ1=sQuery(id+"F2.wireOp",EDGE,"E1");var subQ2=makeQuery(id+"F2.imprint","INTERSECT",VERTEX,{"derivedFrom":[subQ1,subQ0]});Q38=makeQuery(id+"F2.imprint","IMPRINT",FACE,{"disambiguationData":[TD([[makeQuery(id+"F2.imprint","IMPRINT",EDGE,{"disambiguationData":[TD([[subQ2,1.0]])],"derivedFrom":subQ1}),-1.0]])]});}
            var Q39;
            {var subQ0=sQuery(id+"F2.wireOp",EDGE,"E6.3.113.0");var subQ1=sQuery(id+"F2.wireOp",EDGE,"E1");var subQ2=makeQuery(id+"F2.imprint","INTERSECT",VERTEX,{"derivedFrom":[subQ1,subQ0]});Q39=makeQuery(id+"F2.imprint","IMPRINT",FACE,{"disambiguationData":[TD([[makeQuery(id+"F2.imprint","IMPRINT",EDGE,{"disambiguationData":[TD([[subQ2,1.0]])],"derivedFrom":subQ1}),-1.0]])]});}
            var Q40;
            {var subQ0=sQuery(id+"F2.wireOp",EDGE,"E3");var subQ1=sQuery(id+"F2.wireOp",EDGE,"E1");var subQ2=makeQuery(id+"F2.imprint","INTERSECT",VERTEX,{"derivedFrom":[subQ1,subQ0]});Q40=makeQuery(id+"F2.imprint","IMPRINT",FACE,{"disambiguationData":[TD([[makeQuery(id+"F2.imprint","IMPRINT",EDGE,{"disambiguationData":[TD([[subQ2,-1.0]])],"derivedFrom":subQ1}),-1.0]])]});}
            var Q41;
            {var subQ0=sQuery(id+"F2.wireOp",EDGE,"E2");var subQ1=sQuery(id+"F2.wireOp",EDGE,"E1");var subQ2=makeQuery(id+"F2.imprint","INTERSECT",VERTEX,{"derivedFrom":[subQ1,subQ0]});Q41=makeQuery(id+"F2.imprint","IMPRINT",FACE,{"disambiguationData":[TD([[makeQuery(id+"F2.imprint","IMPRINT",EDGE,{"disambiguationData":[TD([[subQ2,1.0]])],"derivedFrom":subQ1}),-1.0]])]});}
            var Q42;
            {var subQ0=sQuery(id+"F2.wireOp",EDGE,"E4.1.1");var subQ1=sQuery(id+"F2.wireOp",EDGE,"E1");var subQ2=makeQuery(id+"F2.imprint","INTERSECT",VERTEX,{"derivedFrom":[subQ1,subQ0]});Q42=makeQuery(id+"F2.imprint","IMPRINT",FACE,{"disambiguationData":[TD([[makeQuery(id+"F2.imprint","IMPRINT",EDGE,{"disambiguationData":[TD([[subQ2,1.0]])],"derivedFrom":subQ1}),-1.0]])]});}
            var Q43;
            {var subQ0=sQuery(id+"F2.wireOp",EDGE,"E4.2.1");var subQ1=sQuery(id+"F2.wireOp",EDGE,"E1");var subQ2=makeQuery(id+"F2.imprint","INTERSECT",VERTEX,{"derivedFrom":[subQ1,subQ0]});Q43=makeQuery(id+"F2.imprint","IMPRINT",FACE,{"disambiguationData":[TD([[makeQuery(id+"F2.imprint","IMPRINT",EDGE,{"disambiguationData":[TD([[subQ2,1.0]])],"derivedFrom":subQ1}),-1.0]])]});}
            var Q44;
            {var subQ0=sQuery(id+"F2.wireOp",EDGE,"E4.3.1");var subQ1=sQuery(id+"F2.wireOp",EDGE,"E1");var subQ2=makeQuery(id+"F2.imprint","INTERSECT",VERTEX,{"derivedFrom":[subQ1,subQ0]});Q44=makeQuery(id+"F2.imprint","IMPRINT",FACE,{"disambiguationData":[TD([[makeQuery(id+"F2.imprint","IMPRINT",EDGE,{"disambiguationData":[TD([[subQ2,1.0]])],"derivedFrom":subQ1}),-1.0]])]});}
            var Q45;
            {var subQ0=sQuery(id+"F2.wireOp",EDGE,"E4.4.1");var subQ1=sQuery(id+"F2.wireOp",EDGE,"E1");var subQ2=makeQuery(id+"F2.imprint","INTERSECT",VERTEX,{"derivedFrom":[subQ1,subQ0]});Q45=makeQuery(id+"F2.imprint","IMPRINT",FACE,{"disambiguationData":[TD([[makeQuery(id+"F2.imprint","IMPRINT",EDGE,{"disambiguationData":[TD([[subQ2,1.0]])],"derivedFrom":subQ1}),-1.0]])]});}
            var Q46;
            {var subQ0=sQuery(id+"F2.wireOp",EDGE,"E4.5.1");var subQ1=sQuery(id+"F2.wireOp",EDGE,"E1");var subQ2=makeQuery(id+"F2.imprint","INTERSECT",VERTEX,{"derivedFrom":[subQ1,subQ0]});Q46=makeQuery(id+"F2.imprint","IMPRINT",FACE,{"disambiguationData":[TD([[makeQuery(id+"F2.imprint","IMPRINT",EDGE,{"disambiguationData":[TD([[subQ2,1.0]])],"derivedFrom":subQ1}),-1.0]])]});}
            var Q47;
            {var subQ0=sQuery(id+"F2.wireOp",EDGE,"E4.6.1");var subQ1=sQuery(id+"F2.wireOp",EDGE,"E1");var subQ2=makeQuery(id+"F2.imprint","INTERSECT",VERTEX,{"derivedFrom":[subQ1,subQ0]});Q47=makeQuery(id+"F2.imprint","IMPRINT",FACE,{"disambiguationData":[TD([[makeQuery(id+"F2.imprint","IMPRINT",EDGE,{"disambiguationData":[TD([[subQ2,1.0]])],"derivedFrom":subQ1}),-1.0]])]});}
            var Q48;
            {var subQ0=sQuery(id+"F2.wireOp",EDGE,"E4.7.1");var subQ1=sQuery(id+"F2.wireOp",EDGE,"E1");var subQ2=makeQuery(id+"F2.imprint","INTERSECT",VERTEX,{"derivedFrom":[subQ1,subQ0]});Q48=makeQuery(id+"F2.imprint","IMPRINT",FACE,{"disambiguationData":[TD([[makeQuery(id+"F2.imprint","IMPRINT",EDGE,{"disambiguationData":[TD([[subQ2,1.0]])],"derivedFrom":subQ1}),-1.0]])]});}
            var Q49;
            {var subQ0=sQuery(id+"F2.wireOp",EDGE,"E4.8.1");var subQ1=sQuery(id+"F2.wireOp",EDGE,"E1");var subQ2=makeQuery(id+"F2.imprint","INTERSECT",VERTEX,{"derivedFrom":[subQ1,subQ0]});Q49=makeQuery(id+"F2.imprint","IMPRINT",FACE,{"disambiguationData":[TD([[makeQuery(id+"F2.imprint","IMPRINT",EDGE,{"disambiguationData":[TD([[subQ2,1.0]])],"derivedFrom":subQ1}),-1.0]])]});}
            var Q50;
            {var subQ0=sQuery(id+"F2.wireOp",EDGE,"E4.9.1");var subQ1=sQuery(id+"F2.wireOp",EDGE,"E1");var subQ2=makeQuery(id+"F2.imprint","INTERSECT",VERTEX,{"derivedFrom":[subQ1,subQ0]});Q50=makeQuery(id+"F2.imprint","IMPRINT",FACE,{"disambiguationData":[TD([[makeQuery(id+"F2.imprint","IMPRINT",EDGE,{"disambiguationData":[TD([[subQ2,1.0]])],"derivedFrom":subQ1}),-1.0]])]});}
            var Q51;
            {var subQ0=sQuery(id+"F2.wireOp",EDGE,"E4.10.1");var subQ1=sQuery(id+"F2.wireOp",EDGE,"E1");var subQ2=makeQuery(id+"F2.imprint","INTERSECT",VERTEX,{"derivedFrom":[subQ1,subQ0]});Q51=makeQuery(id+"F2.imprint","IMPRINT",FACE,{"disambiguationData":[TD([[makeQuery(id+"F2.imprint","IMPRINT",EDGE,{"disambiguationData":[TD([[subQ2,1.0]])],"derivedFrom":subQ1}),-1.0]])]});}
            var Q52;
            {var subQ0=sQuery(id+"F2.wireOp",EDGE,"E4.11.1");var subQ1=sQuery(id+"F2.wireOp",EDGE,"E1");var subQ2=makeQuery(id+"F2.imprint","INTERSECT",VERTEX,{"derivedFrom":[subQ1,subQ0]});Q52=makeQuery(id+"F2.imprint","IMPRINT",FACE,{"disambiguationData":[TD([[makeQuery(id+"F2.imprint","IMPRINT",EDGE,{"disambiguationData":[TD([[subQ2,1.0]])],"derivedFrom":subQ1}),-1.0]])]});}
            var Q53;
            {var subQ0=sQuery(id+"F2.wireOp",EDGE,"E4.12.1");var subQ1=sQuery(id+"F2.wireOp",EDGE,"E1");var subQ2=makeQuery(id+"F2.imprint","INTERSECT",VERTEX,{"derivedFrom":[subQ1,subQ0]});Q53=makeQuery(id+"F2.imprint","IMPRINT",FACE,{"disambiguationData":[TD([[makeQuery(id+"F2.imprint","IMPRINT",EDGE,{"disambiguationData":[TD([[subQ2,1.0]])],"derivedFrom":subQ1}),-1.0]])]});}
            var Q54;
            {var subQ0=sQuery(id+"F2.wireOp",EDGE,"E4.13.1");var subQ1=sQuery(id+"F2.wireOp",EDGE,"E1");var subQ2=makeQuery(id+"F2.imprint","INTERSECT",VERTEX,{"derivedFrom":[subQ1,subQ0]});Q54=makeQuery(id+"F2.imprint","IMPRINT",FACE,{"disambiguationData":[TD([[makeQuery(id+"F2.imprint","IMPRINT",EDGE,{"disambiguationData":[TD([[subQ2,1.0]])],"derivedFrom":subQ1}),-1.0]])]});}
            var Q55;
            {var subQ0=sQuery(id+"F2.wireOp",EDGE,"E4.14.1");var subQ1=sQuery(id+"F2.wireOp",EDGE,"E1");var subQ2=makeQuery(id+"F2.imprint","INTERSECT",VERTEX,{"derivedFrom":[subQ1,subQ0]});Q55=makeQuery(id+"F2.imprint","IMPRINT",FACE,{"disambiguationData":[TD([[makeQuery(id+"F2.imprint","IMPRINT",EDGE,{"disambiguationData":[TD([[subQ2,1.0]])],"derivedFrom":subQ1}),-1.0]])]});}
            var Q56;
            {var subQ0=sQuery(id+"F2.wireOp",EDGE,"E4.15.1");var subQ1=sQuery(id+"F2.wireOp",EDGE,"E1");var subQ2=makeQuery(id+"F2.imprint","INTERSECT",VERTEX,{"derivedFrom":[subQ1,subQ0]});Q56=makeQuery(id+"F2.imprint","IMPRINT",FACE,{"disambiguationData":[TD([[makeQuery(id+"F2.imprint","IMPRINT",EDGE,{"disambiguationData":[TD([[subQ2,1.0]])],"derivedFrom":subQ1}),-1.0]])]});}
            var Q57;
            {var subQ0=sQuery(id+"F2.wireOp",EDGE,"E4.16.1");var subQ1=sQuery(id+"F2.wireOp",EDGE,"E1");var subQ2=makeQuery(id+"F2.imprint","INTERSECT",VERTEX,{"derivedFrom":[subQ1,subQ0]});Q57=makeQuery(id+"F2.imprint","IMPRINT",FACE,{"disambiguationData":[TD([[makeQuery(id+"F2.imprint","IMPRINT",EDGE,{"disambiguationData":[TD([[subQ2,1.0]])],"derivedFrom":subQ1}),-1.0]])]});}
            var Q58;
            {var subQ0=sQuery(id+"F2.wireOp",EDGE,"E4.17.1");var subQ1=sQuery(id+"F2.wireOp",EDGE,"E1");var subQ2=makeQuery(id+"F2.imprint","INTERSECT",VERTEX,{"derivedFrom":[subQ1,subQ0]});Q58=makeQuery(id+"F2.imprint","IMPRINT",FACE,{"disambiguationData":[TD([[makeQuery(id+"F2.imprint","IMPRINT",EDGE,{"disambiguationData":[TD([[subQ2,1.0]])],"derivedFrom":subQ1}),-1.0]])]});}
            var Q59;
            {var subQ0=sQuery(id+"F2.wireOp",EDGE,"E4.18.1");var subQ1=sQuery(id+"F2.wireOp",EDGE,"E1");var subQ2=makeQuery(id+"F2.imprint","INTERSECT",VERTEX,{"derivedFrom":[subQ1,subQ0]});Q59=makeQuery(id+"F2.imprint","IMPRINT",FACE,{"disambiguationData":[TD([[makeQuery(id+"F2.imprint","IMPRINT",EDGE,{"disambiguationData":[TD([[subQ2,1.0]])],"derivedFrom":subQ1}),-1.0]])]});}
            var Q60;
            {var subQ0=sQuery(id+"F2.wireOp",EDGE,"E4.19.1");var subQ1=sQuery(id+"F2.wireOp",EDGE,"E1");var subQ2=makeQuery(id+"F2.imprint","INTERSECT",VERTEX,{"derivedFrom":[subQ1,subQ0]});Q60=makeQuery(id+"F2.imprint","IMPRINT",FACE,{"disambiguationData":[TD([[makeQuery(id+"F2.imprint","IMPRINT",EDGE,{"disambiguationData":[TD([[subQ2,1.0]])],"derivedFrom":subQ1}),-1.0]])]});}
            var Q61;
            {var subQ0=sQuery(id+"F2.wireOp",EDGE,"E4.20.1");var subQ1=sQuery(id+"F2.wireOp",EDGE,"E1");var subQ2=makeQuery(id+"F2.imprint","INTERSECT",VERTEX,{"derivedFrom":[subQ1,subQ0]});Q61=makeQuery(id+"F2.imprint","IMPRINT",FACE,{"disambiguationData":[TD([[makeQuery(id+"F2.imprint","IMPRINT",EDGE,{"disambiguationData":[TD([[subQ2,1.0]])],"derivedFrom":subQ1}),-1.0]])]});}
            var Q62;
            {var subQ0=sQuery(id+"F2.wireOp",EDGE,"E4.21.1");var subQ1=sQuery(id+"F2.wireOp",EDGE,"E1");var subQ2=makeQuery(id+"F2.imprint","INTERSECT",VERTEX,{"derivedFrom":[subQ1,subQ0]});Q62=makeQuery(id+"F2.imprint","IMPRINT",FACE,{"disambiguationData":[TD([[makeQuery(id+"F2.imprint","IMPRINT",EDGE,{"disambiguationData":[TD([[subQ2,1.0]])],"derivedFrom":subQ1}),-1.0]])]});}
            var Q63;
            {var subQ0=sQuery(id+"F2.wireOp",EDGE,"E4.22.1");var subQ1=sQuery(id+"F2.wireOp",EDGE,"E1");var subQ2=makeQuery(id+"F2.imprint","INTERSECT",VERTEX,{"derivedFrom":[subQ1,subQ0]});Q63=makeQuery(id+"F2.imprint","IMPRINT",FACE,{"disambiguationData":[TD([[makeQuery(id+"F2.imprint","IMPRINT",EDGE,{"disambiguationData":[TD([[subQ2,1.0]])],"derivedFrom":subQ1}),-1.0]])]});}
            var Q64;
            {var subQ0=sQuery(id+"F2.wireOp",EDGE,"E4.23.1");var subQ1=sQuery(id+"F2.wireOp",EDGE,"E1");var subQ2=makeQuery(id+"F2.imprint","INTERSECT",VERTEX,{"derivedFrom":[subQ1,subQ0]});Q64=makeQuery(id+"F2.imprint","IMPRINT",FACE,{"disambiguationData":[TD([[makeQuery(id+"F2.imprint","IMPRINT",EDGE,{"disambiguationData":[TD([[subQ2,1.0]])],"derivedFrom":subQ1}),-1.0]])]});}
            var Q65;
            {var subQ0=sQuery(id+"F2.wireOp",EDGE,"E4.24.1");var subQ1=sQuery(id+"F2.wireOp",EDGE,"E1");var subQ2=makeQuery(id+"F2.imprint","INTERSECT",VERTEX,{"derivedFrom":[subQ1,subQ0]});Q65=makeQuery(id+"F2.imprint","IMPRINT",FACE,{"disambiguationData":[TD([[makeQuery(id+"F2.imprint","IMPRINT",EDGE,{"disambiguationData":[TD([[subQ2,1.0]])],"derivedFrom":subQ1}),-1.0]])]});}
            var Q66;
            {var subQ0=sQuery(id+"F2.wireOp",EDGE,"E4.25.1");var subQ1=sQuery(id+"F2.wireOp",EDGE,"E1");var subQ2=makeQuery(id+"F2.imprint","INTERSECT",VERTEX,{"derivedFrom":[subQ1,subQ0]});Q66=makeQuery(id+"F2.imprint","IMPRINT",FACE,{"disambiguationData":[TD([[makeQuery(id+"F2.imprint","IMPRINT",EDGE,{"disambiguationData":[TD([[subQ2,1.0]])],"derivedFrom":subQ1}),-1.0]])]});}
            var Q67;
            {var subQ0=sQuery(id+"F2.wireOp",EDGE,"E4.26.1");var subQ1=sQuery(id+"F2.wireOp",EDGE,"E1");var subQ2=makeQuery(id+"F2.imprint","INTERSECT",VERTEX,{"derivedFrom":[subQ1,subQ0]});Q67=makeQuery(id+"F2.imprint","IMPRINT",FACE,{"disambiguationData":[TD([[makeQuery(id+"F2.imprint","IMPRINT",EDGE,{"disambiguationData":[TD([[subQ2,1.0]])],"derivedFrom":subQ1}),-1.0]])]});}
            var Q68;
            {var subQ0=sQuery(id+"F2.wireOp",EDGE,"E4.27.1");var subQ1=sQuery(id+"F2.wireOp",EDGE,"E1");var subQ2=makeQuery(id+"F2.imprint","INTERSECT",VERTEX,{"derivedFrom":[subQ1,subQ0]});Q68=makeQuery(id+"F2.imprint","IMPRINT",FACE,{"disambiguationData":[TD([[makeQuery(id+"F2.imprint","IMPRINT",EDGE,{"disambiguationData":[TD([[subQ2,1.0]])],"derivedFrom":subQ1}),-1.0]])]});}
            var Q69;
            {var subQ0=sQuery(id+"F2.wireOp",EDGE,"E4.28.1");var subQ1=sQuery(id+"F2.wireOp",EDGE,"E1");var subQ2=makeQuery(id+"F2.imprint","INTERSECT",VERTEX,{"derivedFrom":[subQ1,subQ0]});Q69=makeQuery(id+"F2.imprint","IMPRINT",FACE,{"disambiguationData":[TD([[makeQuery(id+"F2.imprint","IMPRINT",EDGE,{"disambiguationData":[TD([[subQ2,1.0]])],"derivedFrom":subQ1}),-1.0]])]});}
            var Q70;
            {var subQ0=sQuery(id+"F2.wireOp",EDGE,"E4.29.1");var subQ1=sQuery(id+"F2.wireOp",EDGE,"E1");var subQ2=makeQuery(id+"F2.imprint","INTERSECT",VERTEX,{"derivedFrom":[subQ1,subQ0]});Q70=makeQuery(id+"F2.imprint","IMPRINT",FACE,{"disambiguationData":[TD([[makeQuery(id+"F2.imprint","IMPRINT",EDGE,{"disambiguationData":[TD([[subQ2,1.0]])],"derivedFrom":subQ1}),-1.0]])]});}
            var Q71;
            {var subQ0=sQuery(id+"F2.wireOp",EDGE,"E4.30.1");var subQ1=sQuery(id+"F2.wireOp",EDGE,"E1");var subQ2=makeQuery(id+"F2.imprint","INTERSECT",VERTEX,{"derivedFrom":[subQ1,subQ0]});Q71=makeQuery(id+"F2.imprint","IMPRINT",FACE,{"disambiguationData":[TD([[makeQuery(id+"F2.imprint","IMPRINT",EDGE,{"disambiguationData":[TD([[subQ2,1.0]])],"derivedFrom":subQ1}),-1.0]])]});}
            var Q72;
            {var subQ0=sQuery(id+"F2.wireOp",EDGE,"E4.31.1");var subQ1=sQuery(id+"F2.wireOp",EDGE,"E1");var subQ2=makeQuery(id+"F2.imprint","INTERSECT",VERTEX,{"derivedFrom":[subQ1,subQ0]});Q72=makeQuery(id+"F2.imprint","IMPRINT",FACE,{"disambiguationData":[TD([[makeQuery(id+"F2.imprint","IMPRINT",EDGE,{"disambiguationData":[TD([[subQ2,1.0]])],"derivedFrom":subQ1}),-1.0]])]});}
            var Q73;
            {var subQ0=sQuery(id+"F2.wireOp",EDGE,"E4.32.1");var subQ1=sQuery(id+"F2.wireOp",EDGE,"E1");var subQ2=makeQuery(id+"F2.imprint","INTERSECT",VERTEX,{"derivedFrom":[subQ1,subQ0]});Q73=makeQuery(id+"F2.imprint","IMPRINT",FACE,{"disambiguationData":[TD([[makeQuery(id+"F2.imprint","IMPRINT",EDGE,{"disambiguationData":[TD([[subQ2,1.0]])],"derivedFrom":subQ1}),-1.0]])]});}
            var Q74;
            {var subQ0=sQuery(id+"F2.wireOp",EDGE,"E4.33.1");var subQ1=sQuery(id+"F2.wireOp",EDGE,"E1");var subQ2=makeQuery(id+"F2.imprint","INTERSECT",VERTEX,{"derivedFrom":[subQ1,subQ0]});Q74=makeQuery(id+"F2.imprint","IMPRINT",FACE,{"disambiguationData":[TD([[makeQuery(id+"F2.imprint","IMPRINT",EDGE,{"disambiguationData":[TD([[subQ2,1.0]])],"derivedFrom":subQ1}),-1.0]])]});}
            var Q75;
            {var subQ0=sQuery(id+"F2.wireOp",EDGE,"E4.34.1");var subQ1=sQuery(id+"F2.wireOp",EDGE,"E1");var subQ2=makeQuery(id+"F2.imprint","INTERSECT",VERTEX,{"derivedFrom":[subQ1,subQ0]});Q75=makeQuery(id+"F2.imprint","IMPRINT",FACE,{"disambiguationData":[TD([[makeQuery(id+"F2.imprint","IMPRINT",EDGE,{"disambiguationData":[TD([[subQ2,1.0]])],"derivedFrom":subQ1}),-1.0]])]});}
            var Q76;
            {var subQ0=sQuery(id+"F2.wireOp",EDGE,"E4.35.1");var subQ1=sQuery(id+"F2.wireOp",EDGE,"E1");var subQ2=makeQuery(id+"F2.imprint","INTERSECT",VERTEX,{"derivedFrom":[subQ1,subQ0]});Q76=makeQuery(id+"F2.imprint","IMPRINT",FACE,{"disambiguationData":[TD([[makeQuery(id+"F2.imprint","IMPRINT",EDGE,{"disambiguationData":[TD([[subQ2,1.0]])],"derivedFrom":subQ1}),-1.0]])]});}
            var Q77;
            {var subQ0=sQuery(id+"F2.wireOp",EDGE,"E4.36.1");var subQ1=sQuery(id+"F2.wireOp",EDGE,"E1");var subQ2=makeQuery(id+"F2.imprint","INTERSECT",VERTEX,{"derivedFrom":[subQ1,subQ0]});Q77=makeQuery(id+"F2.imprint","IMPRINT",FACE,{"disambiguationData":[TD([[makeQuery(id+"F2.imprint","IMPRINT",EDGE,{"disambiguationData":[TD([[subQ2,1.0]])],"derivedFrom":subQ1}),-1.0]])]});}
            var Q78;
            {var subQ0=sQuery(id+"F2.wireOp",EDGE,"E4.37.1");var subQ1=sQuery(id+"F2.wireOp",EDGE,"E1");var subQ2=makeQuery(id+"F2.imprint","INTERSECT",VERTEX,{"derivedFrom":[subQ1,subQ0]});Q78=makeQuery(id+"F2.imprint","IMPRINT",FACE,{"disambiguationData":[TD([[makeQuery(id+"F2.imprint","IMPRINT",EDGE,{"disambiguationData":[TD([[subQ2,1.0]])],"derivedFrom":subQ1}),-1.0]])]});}
            var Q79;
            {var subQ0=sQuery(id+"F2.wireOp",EDGE,"E4.38.1");var subQ1=sQuery(id+"F2.wireOp",EDGE,"E1");var subQ2=makeQuery(id+"F2.imprint","INTERSECT",VERTEX,{"derivedFrom":[subQ1,subQ0]});Q79=makeQuery(id+"F2.imprint","IMPRINT",FACE,{"disambiguationData":[TD([[makeQuery(id+"F2.imprint","IMPRINT",EDGE,{"disambiguationData":[TD([[subQ2,1.0]])],"derivedFrom":subQ1}),-1.0]])]});}
            var Q80;
            {var subQ0=sQuery(id+"F2.wireOp",EDGE,"E4.39.1");var subQ1=sQuery(id+"F2.wireOp",EDGE,"E1");var subQ2=makeQuery(id+"F2.imprint","INTERSECT",VERTEX,{"derivedFrom":[subQ1,subQ0]});Q80=makeQuery(id+"F2.imprint","IMPRINT",FACE,{"disambiguationData":[TD([[makeQuery(id+"F2.imprint","IMPRINT",EDGE,{"disambiguationData":[TD([[subQ2,1.0]])],"derivedFrom":subQ1}),-1.0]])]});}
            var Q81;
            {var subQ0=sQuery(id+"F2.wireOp",EDGE,"E4.40.1");var subQ1=sQuery(id+"F2.wireOp",EDGE,"E1");var subQ2=makeQuery(id+"F2.imprint","INTERSECT",VERTEX,{"derivedFrom":[subQ1,subQ0]});Q81=makeQuery(id+"F2.imprint","IMPRINT",FACE,{"disambiguationData":[TD([[makeQuery(id+"F2.imprint","IMPRINT",EDGE,{"disambiguationData":[TD([[subQ2,1.0]])],"derivedFrom":subQ1}),-1.0]])]});}
            var Q82;
            {var subQ0=sQuery(id+"F2.wireOp",EDGE,"E4.41.1");var subQ1=sQuery(id+"F2.wireOp",EDGE,"E1");var subQ2=makeQuery(id+"F2.imprint","INTERSECT",VERTEX,{"derivedFrom":[subQ1,subQ0]});Q82=makeQuery(id+"F2.imprint","IMPRINT",FACE,{"disambiguationData":[TD([[makeQuery(id+"F2.imprint","IMPRINT",EDGE,{"disambiguationData":[TD([[subQ2,1.0]])],"derivedFrom":subQ1}),-1.0]])]});}
            var Q83;
            {var subQ0=sQuery(id+"F2.wireOp",EDGE,"E4.42.1");var subQ1=sQuery(id+"F2.wireOp",EDGE,"E1");var subQ2=makeQuery(id+"F2.imprint","INTERSECT",VERTEX,{"derivedFrom":[subQ1,subQ0]});Q83=makeQuery(id+"F2.imprint","IMPRINT",FACE,{"disambiguationData":[TD([[makeQuery(id+"F2.imprint","IMPRINT",EDGE,{"disambiguationData":[TD([[subQ2,1.0]])],"derivedFrom":subQ1}),-1.0]])]});}
            var Q84;
            {var subQ0=sQuery(id+"F2.wireOp",EDGE,"E4.43.1");var subQ1=sQuery(id+"F2.wireOp",EDGE,"E1");var subQ2=makeQuery(id+"F2.imprint","INTERSECT",VERTEX,{"derivedFrom":[subQ1,subQ0]});Q84=makeQuery(id+"F2.imprint","IMPRINT",FACE,{"disambiguationData":[TD([[makeQuery(id+"F2.imprint","IMPRINT",EDGE,{"disambiguationData":[TD([[subQ2,1.0]])],"derivedFrom":subQ1}),-1.0]])]});}
            var Q85;
            {var subQ0=sQuery(id+"F2.wireOp",EDGE,"E4.44.1");var subQ1=sQuery(id+"F2.wireOp",EDGE,"E1");var subQ2=makeQuery(id+"F2.imprint","INTERSECT",VERTEX,{"derivedFrom":[subQ1,subQ0]});Q85=makeQuery(id+"F2.imprint","IMPRINT",FACE,{"disambiguationData":[TD([[makeQuery(id+"F2.imprint","IMPRINT",EDGE,{"disambiguationData":[TD([[subQ2,1.0]])],"derivedFrom":subQ1}),-1.0]])]});}
            var Q86;
            {var subQ0=sQuery(id+"F2.wireOp",EDGE,"E4.45.1");var subQ1=sQuery(id+"F2.wireOp",EDGE,"E1");var subQ2=makeQuery(id+"F2.imprint","INTERSECT",VERTEX,{"derivedFrom":[subQ1,subQ0]});Q86=makeQuery(id+"F2.imprint","IMPRINT",FACE,{"disambiguationData":[TD([[makeQuery(id+"F2.imprint","IMPRINT",EDGE,{"disambiguationData":[TD([[subQ2,1.0]])],"derivedFrom":subQ1}),-1.0]])]});}
            var Q87;
            {var subQ0=sQuery(id+"F2.wireOp",EDGE,"E4.46.1");var subQ1=sQuery(id+"F2.wireOp",EDGE,"E1");var subQ2=makeQuery(id+"F2.imprint","INTERSECT",VERTEX,{"derivedFrom":[subQ1,subQ0]});Q87=makeQuery(id+"F2.imprint","IMPRINT",FACE,{"disambiguationData":[TD([[makeQuery(id+"F2.imprint","IMPRINT",EDGE,{"disambiguationData":[TD([[subQ2,1.0]])],"derivedFrom":subQ1}),-1.0]])]});}
            var Q88;
            {var subQ0=sQuery(id+"F2.wireOp",EDGE,"E4.47.1");var subQ1=sQuery(id+"F2.wireOp",EDGE,"E1");var subQ2=makeQuery(id+"F2.imprint","INTERSECT",VERTEX,{"derivedFrom":[subQ1,subQ0]});Q88=makeQuery(id+"F2.imprint","IMPRINT",FACE,{"disambiguationData":[TD([[makeQuery(id+"F2.imprint","IMPRINT",EDGE,{"disambiguationData":[TD([[subQ2,1.0]])],"derivedFrom":subQ1}),-1.0]])]});}
            var Q89;
            {var subQ0=sQuery(id+"F2.wireOp",EDGE,"E4.48.1");var subQ1=sQuery(id+"F2.wireOp",EDGE,"E1");var subQ2=makeQuery(id+"F2.imprint","INTERSECT",VERTEX,{"derivedFrom":[subQ1,subQ0]});Q89=makeQuery(id+"F2.imprint","IMPRINT",FACE,{"disambiguationData":[TD([[makeQuery(id+"F2.imprint","IMPRINT",EDGE,{"disambiguationData":[TD([[subQ2,1.0]])],"derivedFrom":subQ1}),-1.0]])]});}
            var Q90;
            {var subQ0=sQuery(id+"F2.wireOp",EDGE,"E4.49.1");var subQ1=sQuery(id+"F2.wireOp",EDGE,"E1");var subQ2=makeQuery(id+"F2.imprint","INTERSECT",VERTEX,{"derivedFrom":[subQ1,subQ0]});Q90=makeQuery(id+"F2.imprint","IMPRINT",FACE,{"disambiguationData":[TD([[makeQuery(id+"F2.imprint","IMPRINT",EDGE,{"disambiguationData":[TD([[subQ2,1.0]])],"derivedFrom":subQ1}),-1.0]])]});}
            var Q91;
            {var subQ0=sQuery(id+"F2.wireOp",EDGE,"E4.50.1");var subQ1=sQuery(id+"F2.wireOp",EDGE,"E1");var subQ2=makeQuery(id+"F2.imprint","INTERSECT",VERTEX,{"derivedFrom":[subQ1,subQ0]});Q91=makeQuery(id+"F2.imprint","IMPRINT",FACE,{"disambiguationData":[TD([[makeQuery(id+"F2.imprint","IMPRINT",EDGE,{"disambiguationData":[TD([[subQ2,1.0]])],"derivedFrom":subQ1}),-1.0]])]});}
            var Q92;
            {var subQ0=sQuery(id+"F2.wireOp",EDGE,"E4.51.1");var subQ1=sQuery(id+"F2.wireOp",EDGE,"E1");var subQ2=makeQuery(id+"F2.imprint","INTERSECT",VERTEX,{"derivedFrom":[subQ1,subQ0]});Q92=makeQuery(id+"F2.imprint","IMPRINT",FACE,{"disambiguationData":[TD([[makeQuery(id+"F2.imprint","IMPRINT",EDGE,{"disambiguationData":[TD([[subQ2,1.0]])],"derivedFrom":subQ1}),-1.0]])]});}
            var Q93;
            {var subQ0=sQuery(id+"F2.wireOp",EDGE,"E4.52.1");var subQ1=sQuery(id+"F2.wireOp",EDGE,"E1");var subQ2=makeQuery(id+"F2.imprint","INTERSECT",VERTEX,{"derivedFrom":[subQ1,subQ0]});Q93=makeQuery(id+"F2.imprint","IMPRINT",FACE,{"disambiguationData":[TD([[makeQuery(id+"F2.imprint","IMPRINT",EDGE,{"disambiguationData":[TD([[subQ2,1.0]])],"derivedFrom":subQ1}),-1.0]])]});}
            var Q94;
            {var subQ0=sQuery(id+"F2.wireOp",EDGE,"E4.53.1");var subQ1=sQuery(id+"F2.wireOp",EDGE,"E1");var subQ2=makeQuery(id+"F2.imprint","INTERSECT",VERTEX,{"derivedFrom":[subQ1,subQ0]});Q94=makeQuery(id+"F2.imprint","IMPRINT",FACE,{"disambiguationData":[TD([[makeQuery(id+"F2.imprint","IMPRINT",EDGE,{"disambiguationData":[TD([[subQ2,1.0]])],"derivedFrom":subQ1}),-1.0]])]});}
            var Q95;
            {var subQ0=sQuery(id+"F2.wireOp",EDGE,"E4.54.1");var subQ1=sQuery(id+"F2.wireOp",EDGE,"E1");var subQ2=makeQuery(id+"F2.imprint","INTERSECT",VERTEX,{"derivedFrom":[subQ1,subQ0]});Q95=makeQuery(id+"F2.imprint","IMPRINT",FACE,{"disambiguationData":[TD([[makeQuery(id+"F2.imprint","IMPRINT",EDGE,{"disambiguationData":[TD([[subQ2,1.0]])],"derivedFrom":subQ1}),-1.0]])]});}
            var Q96;
            {var subQ0=sQuery(id+"F2.wireOp",EDGE,"E4.55.1");var subQ1=sQuery(id+"F2.wireOp",EDGE,"E1");var subQ2=makeQuery(id+"F2.imprint","INTERSECT",VERTEX,{"derivedFrom":[subQ1,subQ0]});Q96=makeQuery(id+"F2.imprint","IMPRINT",FACE,{"disambiguationData":[TD([[makeQuery(id+"F2.imprint","IMPRINT",EDGE,{"disambiguationData":[TD([[subQ2,1.0]])],"derivedFrom":subQ1}),-1.0]])]});}
            var Q97;
            {var subQ0=sQuery(id+"F2.wireOp",EDGE,"E4.56.1");var subQ1=sQuery(id+"F2.wireOp",EDGE,"E1");var subQ2=makeQuery(id+"F2.imprint","INTERSECT",VERTEX,{"derivedFrom":[subQ1,subQ0]});Q97=makeQuery(id+"F2.imprint","IMPRINT",FACE,{"disambiguationData":[TD([[makeQuery(id+"F2.imprint","IMPRINT",EDGE,{"disambiguationData":[TD([[subQ2,1.0]])],"derivedFrom":subQ1}),-1.0]])]});}
            var Q98;
            {var subQ0=sQuery(id+"F2.wireOp",EDGE,"E4.57.1");var subQ1=sQuery(id+"F2.wireOp",EDGE,"E1");var subQ2=makeQuery(id+"F2.imprint","INTERSECT",VERTEX,{"derivedFrom":[subQ1,subQ0]});Q98=makeQuery(id+"F2.imprint","IMPRINT",FACE,{"disambiguationData":[TD([[makeQuery(id+"F2.imprint","IMPRINT",EDGE,{"disambiguationData":[TD([[subQ2,1.0]])],"derivedFrom":subQ1}),-1.0]])]});}
            var Q99;
            {var subQ0=sQuery(id+"F2.wireOp",EDGE,"E4.58.1");var subQ1=sQuery(id+"F2.wireOp",EDGE,"E1");var subQ2=makeQuery(id+"F2.imprint","INTERSECT",VERTEX,{"derivedFrom":[subQ1,subQ0]});Q99=makeQuery(id+"F2.imprint","IMPRINT",FACE,{"disambiguationData":[TD([[makeQuery(id+"F2.imprint","IMPRINT",EDGE,{"disambiguationData":[TD([[subQ2,1.0]])],"derivedFrom":subQ1}),-1.0]])]});}
            var Q100;
            {var subQ0=sQuery(id+"F2.wireOp",EDGE,"E4.59.1");var subQ1=sQuery(id+"F2.wireOp",EDGE,"E1");var subQ2=makeQuery(id+"F2.imprint","INTERSECT",VERTEX,{"derivedFrom":[subQ1,subQ0]});Q100=makeQuery(id+"F2.imprint","IMPRINT",FACE,{"disambiguationData":[TD([[makeQuery(id+"F2.imprint","IMPRINT",EDGE,{"disambiguationData":[TD([[subQ2,1.0]])],"derivedFrom":subQ1}),-1.0]])]});}
            var Q101;
            {var subQ0=sQuery(id+"F2.wireOp",EDGE,"E4.60.1");var subQ1=sQuery(id+"F2.wireOp",EDGE,"E1");var subQ2=makeQuery(id+"F2.imprint","INTERSECT",VERTEX,{"derivedFrom":[subQ1,subQ0]});Q101=makeQuery(id+"F2.imprint","IMPRINT",FACE,{"disambiguationData":[TD([[makeQuery(id+"F2.imprint","IMPRINT",EDGE,{"disambiguationData":[TD([[subQ2,1.0]])],"derivedFrom":subQ1}),-1.0]])]});}
            var Q102;
            {var subQ0=sQuery(id+"F2.wireOp",EDGE,"E4.61.1");var subQ1=sQuery(id+"F2.wireOp",EDGE,"E1");var subQ2=makeQuery(id+"F2.imprint","INTERSECT",VERTEX,{"derivedFrom":[subQ1,subQ0]});Q102=makeQuery(id+"F2.imprint","IMPRINT",FACE,{"disambiguationData":[TD([[makeQuery(id+"F2.imprint","IMPRINT",EDGE,{"disambiguationData":[TD([[subQ2,1.0]])],"derivedFrom":subQ1}),-1.0]])]});}
            var Q103;
            {var subQ0=sQuery(id+"F2.wireOp",EDGE,"E4.62.1");var subQ1=sQuery(id+"F2.wireOp",EDGE,"E1");var subQ2=makeQuery(id+"F2.imprint","INTERSECT",VERTEX,{"derivedFrom":[subQ1,subQ0]});Q103=makeQuery(id+"F2.imprint","IMPRINT",FACE,{"disambiguationData":[TD([[makeQuery(id+"F2.imprint","IMPRINT",EDGE,{"disambiguationData":[TD([[subQ2,1.0]])],"derivedFrom":subQ1}),-1.0]])]});}
            var Q104;
            {var subQ0=sQuery(id+"F2.wireOp",EDGE,"E4.63.1");var subQ1=sQuery(id+"F2.wireOp",EDGE,"E1");var subQ2=makeQuery(id+"F2.imprint","INTERSECT",VERTEX,{"derivedFrom":[subQ1,subQ0]});Q104=makeQuery(id+"F2.imprint","IMPRINT",FACE,{"disambiguationData":[TD([[makeQuery(id+"F2.imprint","IMPRINT",EDGE,{"disambiguationData":[TD([[subQ2,1.0]])],"derivedFrom":subQ1}),-1.0]])]});}
            var Q105;
            {var subQ0=sQuery(id+"F2.wireOp",EDGE,"E4.64.1");var subQ1=sQuery(id+"F2.wireOp",EDGE,"E1");var subQ2=makeQuery(id+"F2.imprint","INTERSECT",VERTEX,{"derivedFrom":[subQ1,subQ0]});Q105=makeQuery(id+"F2.imprint","IMPRINT",FACE,{"disambiguationData":[TD([[makeQuery(id+"F2.imprint","IMPRINT",EDGE,{"disambiguationData":[TD([[subQ2,1.0]])],"derivedFrom":subQ1}),-1.0]])]});}
            var Q106;
            {var subQ0=sQuery(id+"F2.wireOp",EDGE,"E4.65.1");var subQ1=sQuery(id+"F2.wireOp",EDGE,"E1");var subQ2=makeQuery(id+"F2.imprint","INTERSECT",VERTEX,{"derivedFrom":[subQ1,subQ0]});Q106=makeQuery(id+"F2.imprint","IMPRINT",FACE,{"disambiguationData":[TD([[makeQuery(id+"F2.imprint","IMPRINT",EDGE,{"disambiguationData":[TD([[subQ2,1.0]])],"derivedFrom":subQ1}),-1.0]])]});}
            var Q107;
            {var subQ0=sQuery(id+"F2.wireOp",EDGE,"E4.66.1");var subQ1=sQuery(id+"F2.wireOp",EDGE,"E1");var subQ2=makeQuery(id+"F2.imprint","INTERSECT",VERTEX,{"derivedFrom":[subQ1,subQ0]});Q107=makeQuery(id+"F2.imprint","IMPRINT",FACE,{"disambiguationData":[TD([[makeQuery(id+"F2.imprint","IMPRINT",EDGE,{"disambiguationData":[TD([[subQ2,1.0]])],"derivedFrom":subQ1}),-1.0]])]});}
            var Q108;
            {var subQ0=sQuery(id+"F2.wireOp",EDGE,"E4.67.1");var subQ1=sQuery(id+"F2.wireOp",EDGE,"E1");var subQ2=makeQuery(id+"F2.imprint","INTERSECT",VERTEX,{"derivedFrom":[subQ1,subQ0]});Q108=makeQuery(id+"F2.imprint","IMPRINT",FACE,{"disambiguationData":[TD([[makeQuery(id+"F2.imprint","IMPRINT",EDGE,{"disambiguationData":[TD([[subQ2,1.0]])],"derivedFrom":subQ1}),-1.0]])]});}
            var Q109;
            {var subQ0=sQuery(id+"F2.wireOp",EDGE,"E4.68.1");var subQ1=sQuery(id+"F2.wireOp",EDGE,"E1");var subQ2=makeQuery(id+"F2.imprint","INTERSECT",VERTEX,{"derivedFrom":[subQ1,subQ0]});Q109=makeQuery(id+"F2.imprint","IMPRINT",FACE,{"disambiguationData":[TD([[makeQuery(id+"F2.imprint","IMPRINT",EDGE,{"disambiguationData":[TD([[subQ2,1.0]])],"derivedFrom":subQ1}),-1.0]])]});}
            var Q110;
            {var subQ0=sQuery(id+"F2.wireOp",EDGE,"E4.69.1");var subQ1=sQuery(id+"F2.wireOp",EDGE,"E1");var subQ2=makeQuery(id+"F2.imprint","INTERSECT",VERTEX,{"derivedFrom":[subQ1,subQ0]});Q110=makeQuery(id+"F2.imprint","IMPRINT",FACE,{"disambiguationData":[TD([[makeQuery(id+"F2.imprint","IMPRINT",EDGE,{"disambiguationData":[TD([[subQ2,1.0]])],"derivedFrom":subQ1}),-1.0]])]});}
            var Q111;
            {var subQ0=sQuery(id+"F2.wireOp",EDGE,"E4.70.1");var subQ1=sQuery(id+"F2.wireOp",EDGE,"E1");var subQ2=makeQuery(id+"F2.imprint","INTERSECT",VERTEX,{"derivedFrom":[subQ1,subQ0]});Q111=makeQuery(id+"F2.imprint","IMPRINT",FACE,{"disambiguationData":[TD([[makeQuery(id+"F2.imprint","IMPRINT",EDGE,{"disambiguationData":[TD([[subQ2,1.0]])],"derivedFrom":subQ1}),-1.0]])]});}
            var Q112;
            {var subQ0=sQuery(id+"F2.wireOp",EDGE,"E4.71.1");var subQ1=sQuery(id+"F2.wireOp",EDGE,"E1");var subQ2=makeQuery(id+"F2.imprint","INTERSECT",VERTEX,{"derivedFrom":[subQ1,subQ0]});Q112=makeQuery(id+"F2.imprint","IMPRINT",FACE,{"disambiguationData":[TD([[makeQuery(id+"F2.imprint","IMPRINT",EDGE,{"disambiguationData":[TD([[subQ2,1.0]])],"derivedFrom":subQ1}),-1.0]])]});}
            var Q113;
            {var subQ0=sQuery(id+"F2.wireOp",EDGE,"E4.72.1");var subQ1=sQuery(id+"F2.wireOp",EDGE,"E1");var subQ2=makeQuery(id+"F2.imprint","INTERSECT",VERTEX,{"derivedFrom":[subQ1,subQ0]});Q113=makeQuery(id+"F2.imprint","IMPRINT",FACE,{"disambiguationData":[TD([[makeQuery(id+"F2.imprint","IMPRINT",EDGE,{"disambiguationData":[TD([[subQ2,1.0]])],"derivedFrom":subQ1}),-1.0]])]});}
            var Q114;
            {var subQ0=sQuery(id+"F2.wireOp",EDGE,"E4.73.1");var subQ1=sQuery(id+"F2.wireOp",EDGE,"E1");var subQ2=makeQuery(id+"F2.imprint","INTERSECT",VERTEX,{"derivedFrom":[subQ1,subQ0]});Q114=makeQuery(id+"F2.imprint","IMPRINT",FACE,{"disambiguationData":[TD([[makeQuery(id+"F2.imprint","IMPRINT",EDGE,{"disambiguationData":[TD([[subQ2,1.0]])],"derivedFrom":subQ1}),-1.0]])]});}
            var Q115;
            {var subQ0=sQuery(id+"F2.wireOp",EDGE,"E4.74.1");var subQ1=sQuery(id+"F2.wireOp",EDGE,"E1");var subQ2=makeQuery(id+"F2.imprint","INTERSECT",VERTEX,{"derivedFrom":[subQ1,subQ0]});Q115=makeQuery(id+"F2.imprint","IMPRINT",FACE,{"disambiguationData":[TD([[makeQuery(id+"F2.imprint","IMPRINT",EDGE,{"disambiguationData":[TD([[subQ2,1.0]])],"derivedFrom":subQ1}),-1.0]])]});}
            var Q116;
            {var subQ0=sQuery(id+"F2.wireOp",EDGE,"E4.75.1");var subQ1=sQuery(id+"F2.wireOp",EDGE,"E1");var subQ2=makeQuery(id+"F2.imprint","INTERSECT",VERTEX,{"derivedFrom":[subQ1,subQ0]});Q116=makeQuery(id+"F2.imprint","IMPRINT",FACE,{"disambiguationData":[TD([[makeQuery(id+"F2.imprint","IMPRINT",EDGE,{"disambiguationData":[TD([[subQ2,1.0]])],"derivedFrom":subQ1}),-1.0]])]});}
            var Q117;
            {var subQ0=sQuery(id+"F2.wireOp",EDGE,"E4.76.1");var subQ1=sQuery(id+"F2.wireOp",EDGE,"E1");var subQ2=makeQuery(id+"F2.imprint","INTERSECT",VERTEX,{"derivedFrom":[subQ1,subQ0]});Q117=makeQuery(id+"F2.imprint","IMPRINT",FACE,{"disambiguationData":[TD([[makeQuery(id+"F2.imprint","IMPRINT",EDGE,{"disambiguationData":[TD([[subQ2,1.0]])],"derivedFrom":subQ1}),-1.0]])]});}
            var Q118;
            {var subQ0=sQuery(id+"F2.wireOp",EDGE,"E4.77.1");var subQ1=sQuery(id+"F2.wireOp",EDGE,"E1");var subQ2=makeQuery(id+"F2.imprint","INTERSECT",VERTEX,{"derivedFrom":[subQ1,subQ0]});Q118=makeQuery(id+"F2.imprint","IMPRINT",FACE,{"disambiguationData":[TD([[makeQuery(id+"F2.imprint","IMPRINT",EDGE,{"disambiguationData":[TD([[subQ2,1.0]])],"derivedFrom":subQ1}),-1.0]])]});}
            var Q119;
            {var subQ0=sQuery(id+"F2.wireOp",EDGE,"E4.78.1");var subQ1=sQuery(id+"F2.wireOp",EDGE,"E1");var subQ2=makeQuery(id+"F2.imprint","INTERSECT",VERTEX,{"derivedFrom":[subQ1,subQ0]});Q119=makeQuery(id+"F2.imprint","IMPRINT",FACE,{"disambiguationData":[TD([[makeQuery(id+"F2.imprint","IMPRINT",EDGE,{"disambiguationData":[TD([[subQ2,1.0]])],"derivedFrom":subQ1}),-1.0]])]});}
            var Q120;
            {var subQ0=sQuery(id+"F2.wireOp",EDGE,"E4.79.1");var subQ1=sQuery(id+"F2.wireOp",EDGE,"E1");var subQ2=makeQuery(id+"F2.imprint","INTERSECT",VERTEX,{"derivedFrom":[subQ1,subQ0]});Q120=makeQuery(id+"F2.imprint","IMPRINT",FACE,{"disambiguationData":[TD([[makeQuery(id+"F2.imprint","IMPRINT",EDGE,{"disambiguationData":[TD([[subQ2,1.0]])],"derivedFrom":subQ1}),-1.0]])]});}
            var Q121;
            {var subQ0=sQuery(id+"F2.wireOp",EDGE,"E4.80.1");var subQ1=sQuery(id+"F2.wireOp",EDGE,"E1");var subQ2=makeQuery(id+"F2.imprint","INTERSECT",VERTEX,{"derivedFrom":[subQ1,subQ0]});Q121=makeQuery(id+"F2.imprint","IMPRINT",FACE,{"disambiguationData":[TD([[makeQuery(id+"F2.imprint","IMPRINT",EDGE,{"disambiguationData":[TD([[subQ2,1.0]])],"derivedFrom":subQ1}),-1.0]])]});}
            var Q122;
            {var subQ0=sQuery(id+"F2.wireOp",EDGE,"E4.81.1");var subQ1=sQuery(id+"F2.wireOp",EDGE,"E1");var subQ2=makeQuery(id+"F2.imprint","INTERSECT",VERTEX,{"derivedFrom":[subQ1,subQ0]});Q122=makeQuery(id+"F2.imprint","IMPRINT",FACE,{"disambiguationData":[TD([[makeQuery(id+"F2.imprint","IMPRINT",EDGE,{"disambiguationData":[TD([[subQ2,1.0]])],"derivedFrom":subQ1}),-1.0]])]});}
            var Q123;
            {var subQ0=sQuery(id+"F2.wireOp",EDGE,"E4.82.1");var subQ1=sQuery(id+"F2.wireOp",EDGE,"E1");var subQ2=makeQuery(id+"F2.imprint","INTERSECT",VERTEX,{"derivedFrom":[subQ1,subQ0]});Q123=makeQuery(id+"F2.imprint","IMPRINT",FACE,{"disambiguationData":[TD([[makeQuery(id+"F2.imprint","IMPRINT",EDGE,{"disambiguationData":[TD([[subQ2,1.0]])],"derivedFrom":subQ1}),-1.0]])]});}
            var Q124;
            {var subQ0=sQuery(id+"F2.wireOp",EDGE,"E4.83.1");var subQ1=sQuery(id+"F2.wireOp",EDGE,"E1");var subQ2=makeQuery(id+"F2.imprint","INTERSECT",VERTEX,{"derivedFrom":[subQ1,subQ0]});Q124=makeQuery(id+"F2.imprint","IMPRINT",FACE,{"disambiguationData":[TD([[makeQuery(id+"F2.imprint","IMPRINT",EDGE,{"disambiguationData":[TD([[subQ2,1.0]])],"derivedFrom":subQ1}),-1.0]])]});}
            var Q125;
            {var subQ0=sQuery(id+"F2.wireOp",EDGE,"E4.84.1");var subQ1=sQuery(id+"F2.wireOp",EDGE,"E1");var subQ2=makeQuery(id+"F2.imprint","INTERSECT",VERTEX,{"derivedFrom":[subQ1,subQ0]});Q125=makeQuery(id+"F2.imprint","IMPRINT",FACE,{"disambiguationData":[TD([[makeQuery(id+"F2.imprint","IMPRINT",EDGE,{"disambiguationData":[TD([[subQ2,1.0]])],"derivedFrom":subQ1}),-1.0]])]});}
            var Q126;
            {var subQ0=sQuery(id+"F2.wireOp",EDGE,"E5.3.85.0");var subQ1=sQuery(id+"F2.wireOp",EDGE,"E1");var subQ2=makeQuery(id+"F2.imprint","INTERSECT",VERTEX,{"derivedFrom":[subQ1,subQ0]});Q126=makeQuery(id+"F2.imprint","IMPRINT",FACE,{"disambiguationData":[TD([[makeQuery(id+"F2.imprint","IMPRINT",EDGE,{"disambiguationData":[TD([[subQ2,1.0]])],"derivedFrom":subQ1}),-1.0]])]});}
            var Q127;
            {var subQ5=sQuery(id+"F2.wireOp",EDGE,"E4.79.1");var subQ7=sQuery(id+"F2.wireOp",EDGE,"E1");var subQ8=makeQuery(id+"F2.imprint","INTERSECT",VERTEX,{"derivedFrom":[subQ7,subQ5]});Q127=makeQuery(id+"F2.imprint","IMPRINT",FACE,{"disambiguationData":[TD([[makeQuery(id+"F2.imprint","IMPRINT",EDGE,{"disambiguationData":[TD([[subQ8,-1.0]])],"derivedFrom":subQ7}),-1.0]])]});}
            var Q128;
            {var subQ5=sQuery(id+"F2.wireOp",EDGE,"E4.49.1");var subQ7=sQuery(id+"F2.wireOp",EDGE,"E1");var subQ8=makeQuery(id+"F2.imprint","INTERSECT",VERTEX,{"derivedFrom":[subQ7,subQ5]});Q128=makeQuery(id+"F2.imprint","IMPRINT",FACE,{"disambiguationData":[TD([[makeQuery(id+"F2.imprint","IMPRINT",EDGE,{"disambiguationData":[TD([[subQ8,-1.0]])],"derivedFrom":subQ7}),-1.0]])]});}
            var Q129;
            {var subQ5=sQuery(id+"F2.wireOp",EDGE,"E4.12.1");var subQ7=sQuery(id+"F2.wireOp",EDGE,"E1");var subQ8=makeQuery(id+"F2.imprint","INTERSECT",VERTEX,{"derivedFrom":[subQ7,subQ5]});Q129=makeQuery(id+"F2.imprint","IMPRINT",FACE,{"disambiguationData":[TD([[makeQuery(id+"F2.imprint","IMPRINT",EDGE,{"disambiguationData":[TD([[subQ8,-1.0]])],"derivedFrom":subQ7}),-1.0]])]});}
            var Q130;
            {var subQ5=sQuery(id+"F2.wireOp",EDGE,"E4.9.1");var subQ7=sQuery(id+"F2.wireOp",EDGE,"E1");var subQ8=makeQuery(id+"F2.imprint","INTERSECT",VERTEX,{"derivedFrom":[subQ7,subQ5]});Q130=makeQuery(id+"F2.imprint","IMPRINT",FACE,{"disambiguationData":[TD([[makeQuery(id+"F2.imprint","IMPRINT",EDGE,{"disambiguationData":[TD([[subQ8,-1.0]])],"derivedFrom":subQ7}),-1.0]])]});}
            var Q131;
            {var subQ5=sQuery(id+"F2.wireOp",EDGE,"E4.16.1");var subQ7=sQuery(id+"F2.wireOp",EDGE,"E1");var subQ8=makeQuery(id+"F2.imprint","INTERSECT",VERTEX,{"derivedFrom":[subQ7,subQ5]});Q131=makeQuery(id+"F2.imprint","IMPRINT",FACE,{"disambiguationData":[TD([[makeQuery(id+"F2.imprint","IMPRINT",EDGE,{"disambiguationData":[TD([[subQ8,-1.0]])],"derivedFrom":subQ7}),-1.0]])]});}
            var Q132;
            {var subQ5=sQuery(id+"F2.wireOp",EDGE,"E4.11.1");var subQ7=sQuery(id+"F2.wireOp",EDGE,"E1");var subQ8=makeQuery(id+"F2.imprint","INTERSECT",VERTEX,{"derivedFrom":[subQ7,subQ5]});Q132=makeQuery(id+"F2.imprint","IMPRINT",FACE,{"disambiguationData":[TD([[makeQuery(id+"F2.imprint","IMPRINT",EDGE,{"disambiguationData":[TD([[subQ8,-1.0]])],"derivedFrom":subQ7}),-1.0]])]});}
            var Q133;
            {var subQ5=sQuery(id+"F2.wireOp",EDGE,"E4.17.1");var subQ7=sQuery(id+"F2.wireOp",EDGE,"E1");var subQ8=makeQuery(id+"F2.imprint","INTERSECT",VERTEX,{"derivedFrom":[subQ7,subQ5]});Q133=makeQuery(id+"F2.imprint","IMPRINT",FACE,{"disambiguationData":[TD([[makeQuery(id+"F2.imprint","IMPRINT",EDGE,{"disambiguationData":[TD([[subQ8,-1.0]])],"derivedFrom":subQ7}),-1.0]])]});}
            var Q134;
            {var subQ5=sQuery(id+"F2.wireOp",EDGE,"E4.18.1");var subQ6=sQuery(id+"F2.wireOp",EDGE,"E1");var subQ7=makeQuery(id+"F2.imprint","INTERSECT",VERTEX,{"derivedFrom":[subQ6,subQ5]});Q134=makeQuery(id+"F2.imprint","IMPRINT",FACE,{"disambiguationData":[TD([[makeQuery(id+"F2.imprint","IMPRINT",EDGE,{"disambiguationData":[TD([[subQ7,-1.0]])],"derivedFrom":subQ6}),-1.0]])]});}
            var Q135;
            {var subQ3=sQuery(id+"F2.wireOp",EDGE,"E4.19.1");var subQ7=sQuery(id+"F2.wireOp",EDGE,"E1");var subQ8=makeQuery(id+"F2.imprint","INTERSECT",VERTEX,{"derivedFrom":[subQ7,subQ3]});Q135=makeQuery(id+"F2.imprint","IMPRINT",FACE,{"disambiguationData":[TD([[makeQuery(id+"F2.imprint","IMPRINT",EDGE,{"disambiguationData":[TD([[subQ8,-1.0]])],"derivedFrom":subQ7}),-1.0]])]});}
            var Q136;
            {var subQ3=sQuery(id+"F2.wireOp",EDGE,"E4.20.1");var subQ5=sQuery(id+"F2.wireOp",EDGE,"E1");var subQ6=makeQuery(id+"F2.imprint","INTERSECT",VERTEX,{"derivedFrom":[subQ5,subQ3]});Q136=makeQuery(id+"F2.imprint","IMPRINT",FACE,{"disambiguationData":[TD([[makeQuery(id+"F2.imprint","IMPRINT",EDGE,{"disambiguationData":[TD([[subQ6,-1.0]])],"derivedFrom":subQ5}),-1.0]])]});}
            var Q137;
            {var subQ5=sQuery(id+"F2.wireOp",EDGE,"E4.21.1");var subQ7=sQuery(id+"F2.wireOp",EDGE,"E1");var subQ8=makeQuery(id+"F2.imprint","INTERSECT",VERTEX,{"derivedFrom":[subQ7,subQ5]});Q137=makeQuery(id+"F2.imprint","IMPRINT",FACE,{"disambiguationData":[TD([[makeQuery(id+"F2.imprint","IMPRINT",EDGE,{"disambiguationData":[TD([[subQ8,-1.0]])],"derivedFrom":subQ7}),-1.0]])]});}
            var Q138;
            {var subQ5=sQuery(id+"F2.wireOp",EDGE,"E4.22.1");var subQ7=sQuery(id+"F2.wireOp",EDGE,"E1");var subQ8=makeQuery(id+"F2.imprint","INTERSECT",VERTEX,{"derivedFrom":[subQ7,subQ5]});Q138=makeQuery(id+"F2.imprint","IMPRINT",FACE,{"disambiguationData":[TD([[makeQuery(id+"F2.imprint","IMPRINT",EDGE,{"disambiguationData":[TD([[subQ8,-1.0]])],"derivedFrom":subQ7}),-1.0]])]});}
            var Q139;
            {var subQ3=sQuery(id+"F2.wireOp",EDGE,"E4.23.1");var subQ5=sQuery(id+"F2.wireOp",EDGE,"E1");var subQ6=makeQuery(id+"F2.imprint","INTERSECT",VERTEX,{"derivedFrom":[subQ5,subQ3]});Q139=makeQuery(id+"F2.imprint","IMPRINT",FACE,{"disambiguationData":[TD([[makeQuery(id+"F2.imprint","IMPRINT",EDGE,{"disambiguationData":[TD([[subQ6,-1.0]])],"derivedFrom":subQ5}),-1.0]])]});}
            var Q140;
            {var subQ5=sQuery(id+"F2.wireOp",EDGE,"E4.24.1");var subQ7=sQuery(id+"F2.wireOp",EDGE,"E1");var subQ8=makeQuery(id+"F2.imprint","INTERSECT",VERTEX,{"derivedFrom":[subQ7,subQ5]});Q140=makeQuery(id+"F2.imprint","IMPRINT",FACE,{"disambiguationData":[TD([[makeQuery(id+"F2.imprint","IMPRINT",EDGE,{"disambiguationData":[TD([[subQ8,-1.0]])],"derivedFrom":subQ7}),-1.0]])]});}
            var Q141;
            {var subQ5=sQuery(id+"F2.wireOp",EDGE,"E4.25.1");var subQ7=sQuery(id+"F2.wireOp",EDGE,"E1");var subQ8=makeQuery(id+"F2.imprint","INTERSECT",VERTEX,{"derivedFrom":[subQ7,subQ5]});Q141=makeQuery(id+"F2.imprint","IMPRINT",FACE,{"disambiguationData":[TD([[makeQuery(id+"F2.imprint","IMPRINT",EDGE,{"disambiguationData":[TD([[subQ8,-1.0]])],"derivedFrom":subQ7}),-1.0]])]});}
            var Q142;
            {var subQ5=sQuery(id+"F2.wireOp",EDGE,"E4.26.1");var subQ7=sQuery(id+"F2.wireOp",EDGE,"E1");var subQ8=makeQuery(id+"F2.imprint","INTERSECT",VERTEX,{"derivedFrom":[subQ7,subQ5]});Q142=makeQuery(id+"F2.imprint","IMPRINT",FACE,{"disambiguationData":[TD([[makeQuery(id+"F2.imprint","IMPRINT",EDGE,{"disambiguationData":[TD([[subQ8,-1.0]])],"derivedFrom":subQ7}),-1.0]])]});}
            var Q143;
            {var subQ5=sQuery(id+"F2.wireOp",EDGE,"E4.27.1");var subQ7=sQuery(id+"F2.wireOp",EDGE,"E1");var subQ8=makeQuery(id+"F2.imprint","INTERSECT",VERTEX,{"derivedFrom":[subQ7,subQ5]});Q143=makeQuery(id+"F2.imprint","IMPRINT",FACE,{"disambiguationData":[TD([[makeQuery(id+"F2.imprint","IMPRINT",EDGE,{"disambiguationData":[TD([[subQ8,-1.0]])],"derivedFrom":subQ7}),-1.0]])]});}
            var Q144;
            {var subQ5=sQuery(id+"F2.wireOp",EDGE,"E4.28.1");var subQ7=sQuery(id+"F2.wireOp",EDGE,"E1");var subQ8=makeQuery(id+"F2.imprint","INTERSECT",VERTEX,{"derivedFrom":[subQ7,subQ5]});Q144=makeQuery(id+"F2.imprint","IMPRINT",FACE,{"disambiguationData":[TD([[makeQuery(id+"F2.imprint","IMPRINT",EDGE,{"disambiguationData":[TD([[subQ8,-1.0]])],"derivedFrom":subQ7}),-1.0]])]});}
            var Q145;
            {var subQ5=sQuery(id+"F2.wireOp",EDGE,"E4.29.1");var subQ7=sQuery(id+"F2.wireOp",EDGE,"E1");var subQ8=makeQuery(id+"F2.imprint","INTERSECT",VERTEX,{"derivedFrom":[subQ7,subQ5]});Q145=makeQuery(id+"F2.imprint","IMPRINT",FACE,{"disambiguationData":[TD([[makeQuery(id+"F2.imprint","IMPRINT",EDGE,{"disambiguationData":[TD([[subQ8,-1.0]])],"derivedFrom":subQ7}),-1.0]])]});}
            var Q146;
            {var subQ5=sQuery(id+"F2.wireOp",EDGE,"E4.31.1");var subQ6=sQuery(id+"F2.wireOp",EDGE,"E1");var subQ7=makeQuery(id+"F2.imprint","INTERSECT",VERTEX,{"derivedFrom":[subQ6,subQ5]});Q146=makeQuery(id+"F2.imprint","IMPRINT",FACE,{"disambiguationData":[TD([[makeQuery(id+"F2.imprint","IMPRINT",EDGE,{"disambiguationData":[TD([[subQ7,-1.0]])],"derivedFrom":subQ6}),-1.0]])]});}
            var Q147;
            {var subQ5=sQuery(id+"F2.wireOp",EDGE,"E4.32.1");var subQ6=sQuery(id+"F2.wireOp",EDGE,"E1");var subQ7=makeQuery(id+"F2.imprint","INTERSECT",VERTEX,{"derivedFrom":[subQ6,subQ5]});Q147=makeQuery(id+"F2.imprint","IMPRINT",FACE,{"disambiguationData":[TD([[makeQuery(id+"F2.imprint","IMPRINT",EDGE,{"disambiguationData":[TD([[subQ7,-1.0]])],"derivedFrom":subQ6}),-1.0]])]});}
            var Q148;
            {var subQ5=sQuery(id+"F2.wireOp",EDGE,"E4.33.1");var subQ7=sQuery(id+"F2.wireOp",EDGE,"E1");var subQ8=makeQuery(id+"F2.imprint","INTERSECT",VERTEX,{"derivedFrom":[subQ7,subQ5]});Q148=makeQuery(id+"F2.imprint","IMPRINT",FACE,{"disambiguationData":[TD([[makeQuery(id+"F2.imprint","IMPRINT",EDGE,{"disambiguationData":[TD([[subQ8,-1.0]])],"derivedFrom":subQ7}),-1.0]])]});}
            var Q149;
            {var subQ5=sQuery(id+"F2.wireOp",EDGE,"E4.35.1");var subQ7=sQuery(id+"F2.wireOp",EDGE,"E1");var subQ8=makeQuery(id+"F2.imprint","INTERSECT",VERTEX,{"derivedFrom":[subQ7,subQ5]});Q149=makeQuery(id+"F2.imprint","IMPRINT",FACE,{"disambiguationData":[TD([[makeQuery(id+"F2.imprint","IMPRINT",EDGE,{"disambiguationData":[TD([[subQ8,-1.0]])],"derivedFrom":subQ7}),-1.0]])]});}
            var Q150;
            {var subQ5=sQuery(id+"F2.wireOp",EDGE,"E4.40.1");var subQ7=sQuery(id+"F2.wireOp",EDGE,"E1");var subQ8=makeQuery(id+"F2.imprint","INTERSECT",VERTEX,{"derivedFrom":[subQ7,subQ5]});Q150=makeQuery(id+"F2.imprint","IMPRINT",FACE,{"disambiguationData":[TD([[makeQuery(id+"F2.imprint","IMPRINT",EDGE,{"disambiguationData":[TD([[subQ8,-1.0]])],"derivedFrom":subQ7}),-1.0]])]});}
            var Q151;
            {var subQ5=sQuery(id+"F2.wireOp",EDGE,"E4.84.1");var subQ7=sQuery(id+"F2.wireOp",EDGE,"E1");var subQ8=makeQuery(id+"F2.imprint","INTERSECT",VERTEX,{"derivedFrom":[subQ7,subQ5]});Q151=makeQuery(id+"F2.imprint","IMPRINT",FACE,{"disambiguationData":[TD([[makeQuery(id+"F2.imprint","IMPRINT",EDGE,{"disambiguationData":[TD([[subQ8,-1.0]])],"derivedFrom":subQ7}),-1.0]])]});}
            var Q152;
            {var subQ5=sQuery(id+"F2.wireOp",EDGE,"E4.41.1");var subQ6=sQuery(id+"F2.wireOp",EDGE,"E1");var subQ7=makeQuery(id+"F2.imprint","INTERSECT",VERTEX,{"derivedFrom":[subQ6,subQ5]});Q152=makeQuery(id+"F2.imprint","IMPRINT",FACE,{"disambiguationData":[TD([[makeQuery(id+"F2.imprint","IMPRINT",EDGE,{"disambiguationData":[TD([[subQ7,-1.0]])],"derivedFrom":subQ6}),-1.0]])]});}
            var Q153;
            {var subQ5=sQuery(id+"F2.wireOp",EDGE,"E4.42.1");var subQ7=sQuery(id+"F2.wireOp",EDGE,"E1");var subQ8=makeQuery(id+"F2.imprint","INTERSECT",VERTEX,{"derivedFrom":[subQ7,subQ5]});Q153=makeQuery(id+"F2.imprint","IMPRINT",FACE,{"disambiguationData":[TD([[makeQuery(id+"F2.imprint","IMPRINT",EDGE,{"disambiguationData":[TD([[subQ8,-1.0]])],"derivedFrom":subQ7}),-1.0]])]});}
            var Q154;
            {var subQ5=sQuery(id+"F2.wireOp",EDGE,"E4.81.1");var subQ7=sQuery(id+"F2.wireOp",EDGE,"E1");var subQ8=makeQuery(id+"F2.imprint","INTERSECT",VERTEX,{"derivedFrom":[subQ7,subQ5]});Q154=makeQuery(id+"F2.imprint","IMPRINT",FACE,{"disambiguationData":[TD([[makeQuery(id+"F2.imprint","IMPRINT",EDGE,{"disambiguationData":[TD([[subQ8,-1.0]])],"derivedFrom":subQ7}),-1.0]])]});}
            var Q155;
            {var subQ5=sQuery(id+"F2.wireOp",EDGE,"E4.43.1");var subQ7=sQuery(id+"F2.wireOp",EDGE,"E1");var subQ8=makeQuery(id+"F2.imprint","INTERSECT",VERTEX,{"derivedFrom":[subQ7,subQ5]});Q155=makeQuery(id+"F2.imprint","IMPRINT",FACE,{"disambiguationData":[TD([[makeQuery(id+"F2.imprint","IMPRINT",EDGE,{"disambiguationData":[TD([[subQ8,-1.0]])],"derivedFrom":subQ7}),-1.0]])]});}
            var Q156;
            {var subQ5=sQuery(id+"F2.wireOp",EDGE,"E4.80.1");var subQ7=sQuery(id+"F2.wireOp",EDGE,"E1");var subQ9=makeQuery(id+"F2.imprint","INTERSECT",VERTEX,{"derivedFrom":[subQ7,subQ5]});Q156=makeQuery(id+"F2.imprint","IMPRINT",FACE,{"disambiguationData":[TD([[makeQuery(id+"F2.imprint","IMPRINT",EDGE,{"disambiguationData":[TD([[subQ9,-1.0]])],"derivedFrom":subQ7}),-1.0]])]});}
            var Q157;
            {var subQ5=sQuery(id+"F2.wireOp",EDGE,"E4.44.1");var subQ7=sQuery(id+"F2.wireOp",EDGE,"E1");var subQ8=makeQuery(id+"F2.imprint","INTERSECT",VERTEX,{"derivedFrom":[subQ7,subQ5]});Q157=makeQuery(id+"F2.imprint","IMPRINT",FACE,{"disambiguationData":[TD([[makeQuery(id+"F2.imprint","IMPRINT",EDGE,{"disambiguationData":[TD([[subQ8,-1.0]])],"derivedFrom":subQ7}),-1.0]])]});}
            var Q158;
            {var subQ5=sQuery(id+"F2.wireOp",EDGE,"E4.45.1");var subQ7=sQuery(id+"F2.wireOp",EDGE,"E1");var subQ8=makeQuery(id+"F2.imprint","INTERSECT",VERTEX,{"derivedFrom":[subQ7,subQ5]});Q158=makeQuery(id+"F2.imprint","IMPRINT",FACE,{"disambiguationData":[TD([[makeQuery(id+"F2.imprint","IMPRINT",EDGE,{"disambiguationData":[TD([[subQ8,-1.0]])],"derivedFrom":subQ7}),-1.0]])]});}
            var Q159;
            {var subQ5=sQuery(id+"F2.wireOp",EDGE,"E4.78.1");var subQ7=sQuery(id+"F2.wireOp",EDGE,"E1");var subQ8=makeQuery(id+"F2.imprint","INTERSECT",VERTEX,{"derivedFrom":[subQ7,subQ5]});Q159=makeQuery(id+"F2.imprint","IMPRINT",FACE,{"disambiguationData":[TD([[makeQuery(id+"F2.imprint","IMPRINT",EDGE,{"disambiguationData":[TD([[subQ8,-1.0]])],"derivedFrom":subQ7}),-1.0]])]});}
            var Q160;
            {var subQ5=sQuery(id+"F2.wireOp",EDGE,"E4.46.1");var subQ7=sQuery(id+"F2.wireOp",EDGE,"E1");var subQ8=makeQuery(id+"F2.imprint","INTERSECT",VERTEX,{"derivedFrom":[subQ7,subQ5]});Q160=makeQuery(id+"F2.imprint","IMPRINT",FACE,{"disambiguationData":[TD([[makeQuery(id+"F2.imprint","IMPRINT",EDGE,{"disambiguationData":[TD([[subQ8,-1.0]])],"derivedFrom":subQ7}),-1.0]])]});}
            var Q161;
            {var subQ5=sQuery(id+"F2.wireOp",EDGE,"E4.77.1");var subQ7=sQuery(id+"F2.wireOp",EDGE,"E1");var subQ8=makeQuery(id+"F2.imprint","INTERSECT",VERTEX,{"derivedFrom":[subQ7,subQ5]});Q161=makeQuery(id+"F2.imprint","IMPRINT",FACE,{"disambiguationData":[TD([[makeQuery(id+"F2.imprint","IMPRINT",EDGE,{"disambiguationData":[TD([[subQ8,-1.0]])],"derivedFrom":subQ7}),-1.0]])]});}
            var Q162;
            {var subQ5=sQuery(id+"F2.wireOp",EDGE,"E4.47.1");var subQ7=sQuery(id+"F2.wireOp",EDGE,"E1");var subQ8=makeQuery(id+"F2.imprint","INTERSECT",VERTEX,{"derivedFrom":[subQ7,subQ5]});Q162=makeQuery(id+"F2.imprint","IMPRINT",FACE,{"disambiguationData":[TD([[makeQuery(id+"F2.imprint","IMPRINT",EDGE,{"disambiguationData":[TD([[subQ8,-1.0]])],"derivedFrom":subQ7}),-1.0]])]});}
            var Q163;
            {var subQ5=sQuery(id+"F2.wireOp",EDGE,"E4.48.1");var subQ7=sQuery(id+"F2.wireOp",EDGE,"E1");var subQ8=makeQuery(id+"F2.imprint","INTERSECT",VERTEX,{"derivedFrom":[subQ7,subQ5]});Q163=makeQuery(id+"F2.imprint","IMPRINT",FACE,{"disambiguationData":[TD([[makeQuery(id+"F2.imprint","IMPRINT",EDGE,{"disambiguationData":[TD([[subQ8,-1.0]])],"derivedFrom":subQ7}),-1.0]])]});}
            var Q164;
            {var subQ5=sQuery(id+"F2.wireOp",EDGE,"E4.76.1");var subQ7=sQuery(id+"F2.wireOp",EDGE,"E1");var subQ8=makeQuery(id+"F2.imprint","INTERSECT",VERTEX,{"derivedFrom":[subQ7,subQ5]});Q164=makeQuery(id+"F2.imprint","IMPRINT",FACE,{"disambiguationData":[TD([[makeQuery(id+"F2.imprint","IMPRINT",EDGE,{"disambiguationData":[TD([[subQ8,-1.0]])],"derivedFrom":subQ7}),-1.0]])]});}
            var Q165;
            {var subQ3=sQuery(id+"F2.wireOp",EDGE,"E4.75.1");var subQ7=sQuery(id+"F2.wireOp",EDGE,"E1");var subQ8=makeQuery(id+"F2.imprint","INTERSECT",VERTEX,{"derivedFrom":[subQ7,subQ3]});Q165=makeQuery(id+"F2.imprint","IMPRINT",FACE,{"disambiguationData":[TD([[makeQuery(id+"F2.imprint","IMPRINT",EDGE,{"disambiguationData":[TD([[subQ8,-1.0]])],"derivedFrom":subQ7}),-1.0]])]});}
            var Q166;
            {var subQ3=sQuery(id+"F2.wireOp",EDGE,"E4.50.1");var subQ7=sQuery(id+"F2.wireOp",EDGE,"E1");var subQ8=makeQuery(id+"F2.imprint","INTERSECT",VERTEX,{"derivedFrom":[subQ7,subQ3]});Q166=makeQuery(id+"F2.imprint","IMPRINT",FACE,{"disambiguationData":[TD([[makeQuery(id+"F2.imprint","IMPRINT",EDGE,{"disambiguationData":[TD([[subQ8,-1.0]])],"derivedFrom":subQ7}),-1.0]])]});}
            var Q167;
            {var subQ5=sQuery(id+"F2.wireOp",EDGE,"E4.74.1");var subQ7=sQuery(id+"F2.wireOp",EDGE,"E1");var subQ8=makeQuery(id+"F2.imprint","INTERSECT",VERTEX,{"derivedFrom":[subQ7,subQ5]});Q167=makeQuery(id+"F2.imprint","IMPRINT",FACE,{"disambiguationData":[TD([[makeQuery(id+"F2.imprint","IMPRINT",EDGE,{"disambiguationData":[TD([[subQ8,-1.0]])],"derivedFrom":subQ7}),-1.0]])]});}
            var Q168;
            {var subQ3=sQuery(id+"F2.wireOp",EDGE,"E4.73.1");var subQ5=sQuery(id+"F2.wireOp",EDGE,"E1");var subQ6=makeQuery(id+"F2.imprint","INTERSECT",VERTEX,{"derivedFrom":[subQ5,subQ3]});Q168=makeQuery(id+"F2.imprint","IMPRINT",FACE,{"disambiguationData":[TD([[makeQuery(id+"F2.imprint","IMPRINT",EDGE,{"disambiguationData":[TD([[subQ6,-1.0]])],"derivedFrom":subQ5}),-1.0]])]});}
            var Q169;
            {var subQ5=sQuery(id+"F2.wireOp",EDGE,"E4.52.1");var subQ7=sQuery(id+"F2.wireOp",EDGE,"E1");var subQ8=makeQuery(id+"F2.imprint","INTERSECT",VERTEX,{"derivedFrom":[subQ7,subQ5]});Q169=makeQuery(id+"F2.imprint","IMPRINT",FACE,{"disambiguationData":[TD([[makeQuery(id+"F2.imprint","IMPRINT",EDGE,{"disambiguationData":[TD([[subQ8,-1.0]])],"derivedFrom":subQ7}),-1.0]])]});}
            var Q170;
            {var subQ5=sQuery(id+"F2.wireOp",EDGE,"E4.51.1");var subQ7=sQuery(id+"F2.wireOp",EDGE,"E1");var subQ8=makeQuery(id+"F2.imprint","INTERSECT",VERTEX,{"derivedFrom":[subQ7,subQ5]});Q170=makeQuery(id+"F2.imprint","IMPRINT",FACE,{"disambiguationData":[TD([[makeQuery(id+"F2.imprint","IMPRINT",EDGE,{"disambiguationData":[TD([[subQ8,-1.0]])],"derivedFrom":subQ7}),-1.0]])]});}
            var Q171;
            {var subQ3=sQuery(id+"F2.wireOp",EDGE,"E4.72.1");var subQ5=sQuery(id+"F2.wireOp",EDGE,"E1");var subQ6=makeQuery(id+"F2.imprint","INTERSECT",VERTEX,{"derivedFrom":[subQ5,subQ3]});Q171=makeQuery(id+"F2.imprint","IMPRINT",FACE,{"disambiguationData":[TD([[makeQuery(id+"F2.imprint","IMPRINT",EDGE,{"disambiguationData":[TD([[subQ6,-1.0]])],"derivedFrom":subQ5}),-1.0]])]});}
            var Q172;
            {var subQ5=sQuery(id+"F2.wireOp",EDGE,"E4.71.1");var subQ7=sQuery(id+"F2.wireOp",EDGE,"E1");var subQ8=makeQuery(id+"F2.imprint","INTERSECT",VERTEX,{"derivedFrom":[subQ7,subQ5]});Q172=makeQuery(id+"F2.imprint","IMPRINT",FACE,{"disambiguationData":[TD([[makeQuery(id+"F2.imprint","IMPRINT",EDGE,{"disambiguationData":[TD([[subQ8,-1.0]])],"derivedFrom":subQ7}),-1.0]])]});}
            var Q173;
            {var subQ5=sQuery(id+"F2.wireOp",EDGE,"E4.54.1");var subQ7=sQuery(id+"F2.wireOp",EDGE,"E1");var subQ8=makeQuery(id+"F2.imprint","INTERSECT",VERTEX,{"derivedFrom":[subQ7,subQ5]});Q173=makeQuery(id+"F2.imprint","IMPRINT",FACE,{"disambiguationData":[TD([[makeQuery(id+"F2.imprint","IMPRINT",EDGE,{"disambiguationData":[TD([[subQ8,-1.0]])],"derivedFrom":subQ7}),-1.0]])]});}
            var Q174;
            {var subQ0=sQuery(id+"F2.wireOp",EDGE,"E4.53.1");var subQ1=sQuery(id+"F2.wireOp",EDGE,"E1");var subQ2=makeQuery(id+"F2.imprint","INTERSECT",VERTEX,{"derivedFrom":[subQ1,subQ0]});Q174=makeQuery(id+"F2.imprint","IMPRINT",FACE,{"disambiguationData":[TD([[makeQuery(id+"F2.imprint","IMPRINT",EDGE,{"disambiguationData":[TD([[subQ2,-1.0]])],"derivedFrom":subQ1}),-1.0]])]});}
            var Q175;
            {var subQ5=sQuery(id+"F2.wireOp",EDGE,"E4.70.1");var subQ7=sQuery(id+"F2.wireOp",EDGE,"E1");var subQ8=makeQuery(id+"F2.imprint","INTERSECT",VERTEX,{"derivedFrom":[subQ7,subQ5]});Q175=makeQuery(id+"F2.imprint","IMPRINT",FACE,{"disambiguationData":[TD([[makeQuery(id+"F2.imprint","IMPRINT",EDGE,{"disambiguationData":[TD([[subQ8,-1.0]])],"derivedFrom":subQ7}),-1.0]])]});}
            var Q176;
            {var subQ5=sQuery(id+"F2.wireOp",EDGE,"E4.55.1");var subQ7=sQuery(id+"F2.wireOp",EDGE,"E1");var subQ8=makeQuery(id+"F2.imprint","INTERSECT",VERTEX,{"derivedFrom":[subQ7,subQ5]});Q176=makeQuery(id+"F2.imprint","IMPRINT",FACE,{"disambiguationData":[TD([[makeQuery(id+"F2.imprint","IMPRINT",EDGE,{"disambiguationData":[TD([[subQ8,-1.0]])],"derivedFrom":subQ7}),-1.0]])]});}
            var Q177;
            {var subQ5=sQuery(id+"F2.wireOp",EDGE,"E4.56.1");var subQ7=sQuery(id+"F2.wireOp",EDGE,"E1");var subQ8=makeQuery(id+"F2.imprint","INTERSECT",VERTEX,{"derivedFrom":[subQ7,subQ5]});Q177=makeQuery(id+"F2.imprint","IMPRINT",FACE,{"disambiguationData":[TD([[makeQuery(id+"F2.imprint","IMPRINT",EDGE,{"disambiguationData":[TD([[subQ8,-1.0]])],"derivedFrom":subQ7}),-1.0]])]});}
            var Q178;
            {var subQ5=sQuery(id+"F2.wireOp",EDGE,"E4.68.1");var subQ6=sQuery(id+"F2.wireOp",EDGE,"E1");var subQ7=makeQuery(id+"F2.imprint","INTERSECT",VERTEX,{"derivedFrom":[subQ6,subQ5]});Q178=makeQuery(id+"F2.imprint","IMPRINT",FACE,{"disambiguationData":[TD([[makeQuery(id+"F2.imprint","IMPRINT",EDGE,{"disambiguationData":[TD([[subQ7,-1.0]])],"derivedFrom":subQ6}),-1.0]])]});}
            var Q179;
            {var subQ5=sQuery(id+"F2.wireOp",EDGE,"E4.67.1");var subQ7=sQuery(id+"F2.wireOp",EDGE,"E1");var subQ8=makeQuery(id+"F2.imprint","INTERSECT",VERTEX,{"derivedFrom":[subQ7,subQ5]});Q179=makeQuery(id+"F2.imprint","IMPRINT",FACE,{"disambiguationData":[TD([[makeQuery(id+"F2.imprint","IMPRINT",EDGE,{"disambiguationData":[TD([[subQ8,-1.0]])],"derivedFrom":subQ7}),-1.0]])]});}
            var Q180;
            {var subQ3=sQuery(id+"F2.wireOp",EDGE,"E4.66.1");var subQ7=sQuery(id+"F2.wireOp",EDGE,"E1");var subQ8=makeQuery(id+"F2.imprint","INTERSECT",VERTEX,{"derivedFrom":[subQ7,subQ3]});Q180=makeQuery(id+"F2.imprint","IMPRINT",FACE,{"disambiguationData":[TD([[makeQuery(id+"F2.imprint","IMPRINT",EDGE,{"disambiguationData":[TD([[subQ8,-1.0]])],"derivedFrom":subQ7}),-1.0]])]});}
            var Q181;
            {var subQ3=sQuery(id+"F2.wireOp",EDGE,"E4.65.1");var subQ5=sQuery(id+"F2.wireOp",EDGE,"E1");var subQ6=makeQuery(id+"F2.imprint","INTERSECT",VERTEX,{"derivedFrom":[subQ5,subQ3]});Q181=makeQuery(id+"F2.imprint","IMPRINT",FACE,{"disambiguationData":[TD([[makeQuery(id+"F2.imprint","IMPRINT",EDGE,{"disambiguationData":[TD([[subQ6,-1.0]])],"derivedFrom":subQ5}),-1.0]])]});}
            var Q182;
            {var subQ5=sQuery(id+"F2.wireOp",EDGE,"E4.64.1");var subQ7=sQuery(id+"F2.wireOp",EDGE,"E1");var subQ8=makeQuery(id+"F2.imprint","INTERSECT",VERTEX,{"derivedFrom":[subQ7,subQ5]});Q182=makeQuery(id+"F2.imprint","IMPRINT",FACE,{"disambiguationData":[TD([[makeQuery(id+"F2.imprint","IMPRINT",EDGE,{"disambiguationData":[TD([[subQ8,-1.0]])],"derivedFrom":subQ7}),-1.0]])]});}
            var Q183;
            {var subQ5=sQuery(id+"F2.wireOp",EDGE,"E4.61.1");var subQ7=sQuery(id+"F2.wireOp",EDGE,"E1");var subQ8=makeQuery(id+"F2.imprint","INTERSECT",VERTEX,{"derivedFrom":[subQ7,subQ5]});Q183=makeQuery(id+"F2.imprint","IMPRINT",FACE,{"disambiguationData":[TD([[makeQuery(id+"F2.imprint","IMPRINT",EDGE,{"disambiguationData":[TD([[subQ8,-1.0]])],"derivedFrom":subQ7}),-1.0]])]});}
            var Q184;
            {var subQ3=sQuery(id+"F2.wireOp",EDGE,"E4.60.1");var subQ5=sQuery(id+"F2.wireOp",EDGE,"E1");var subQ6=makeQuery(id+"F2.imprint","INTERSECT",VERTEX,{"derivedFrom":[subQ5,subQ3]});Q184=makeQuery(id+"F2.imprint","IMPRINT",FACE,{"disambiguationData":[TD([[makeQuery(id+"F2.imprint","IMPRINT",EDGE,{"disambiguationData":[TD([[subQ6,-1.0]])],"derivedFrom":subQ5}),-1.0]])]});}
            var Q185;
            {var subQ5=sQuery(id+"F2.wireOp",EDGE,"E4.59.1");var subQ7=sQuery(id+"F2.wireOp",EDGE,"E1");var subQ8=makeQuery(id+"F2.imprint","INTERSECT",VERTEX,{"derivedFrom":[subQ7,subQ5]});Q185=makeQuery(id+"F2.imprint","IMPRINT",FACE,{"disambiguationData":[TD([[makeQuery(id+"F2.imprint","IMPRINT",EDGE,{"disambiguationData":[TD([[subQ8,-1.0]])],"derivedFrom":subQ7}),-1.0]])]});}
            var Q186;
            {var subQ5=sQuery(id+"F2.wireOp",EDGE,"E4.13.1");var subQ7=sQuery(id+"F2.wireOp",EDGE,"E1");var subQ8=makeQuery(id+"F2.imprint","INTERSECT",VERTEX,{"derivedFrom":[subQ7,subQ5]});Q186=makeQuery(id+"F2.imprint","IMPRINT",FACE,{"disambiguationData":[TD([[makeQuery(id+"F2.imprint","IMPRINT",EDGE,{"disambiguationData":[TD([[subQ8,-1.0]])],"derivedFrom":subQ7}),-1.0]])]});}
            var Q187;
            {var subQ5=sQuery(id+"F2.wireOp",EDGE,"E4.14.1");var subQ7=sQuery(id+"F2.wireOp",EDGE,"E1");var subQ8=makeQuery(id+"F2.imprint","INTERSECT",VERTEX,{"derivedFrom":[subQ7,subQ5]});Q187=makeQuery(id+"F2.imprint","IMPRINT",FACE,{"disambiguationData":[TD([[makeQuery(id+"F2.imprint","IMPRINT",EDGE,{"disambiguationData":[TD([[subQ8,-1.0]])],"derivedFrom":subQ7}),-1.0]])]});}
            var Q188;
            {var subQ5=sQuery(id+"F2.wireOp",EDGE,"E4.10.1");var subQ6=sQuery(id+"F2.wireOp",EDGE,"E1");var subQ7=makeQuery(id+"F2.imprint","INTERSECT",VERTEX,{"derivedFrom":[subQ6,subQ5]});Q188=makeQuery(id+"F2.imprint","IMPRINT",FACE,{"disambiguationData":[TD([[makeQuery(id+"F2.imprint","IMPRINT",EDGE,{"disambiguationData":[TD([[subQ7,-1.0]])],"derivedFrom":subQ6}),-1.0]])]});}
            var Q189;
            {var subQ5=sQuery(id+"F2.wireOp",EDGE,"E4.15.1");var subQ7=sQuery(id+"F2.wireOp",EDGE,"E1");var subQ8=makeQuery(id+"F2.imprint","INTERSECT",VERTEX,{"derivedFrom":[subQ7,subQ5]});Q189=makeQuery(id+"F2.imprint","IMPRINT",FACE,{"disambiguationData":[TD([[makeQuery(id+"F2.imprint","IMPRINT",EDGE,{"disambiguationData":[TD([[subQ8,-1.0]])],"derivedFrom":subQ7}),-1.0]])]});}
            var Q190;
            {var subQ5=sQuery(id+"F2.wireOp",EDGE,"E4.30.1");var subQ7=sQuery(id+"F2.wireOp",EDGE,"E1");var subQ8=makeQuery(id+"F2.imprint","INTERSECT",VERTEX,{"derivedFrom":[subQ7,subQ5]});Q190=makeQuery(id+"F2.imprint","IMPRINT",FACE,{"disambiguationData":[TD([[makeQuery(id+"F2.imprint","IMPRINT",EDGE,{"disambiguationData":[TD([[subQ8,-1.0]])],"derivedFrom":subQ7}),-1.0]])]});}
            var Q191;
            {var subQ5=sQuery(id+"F2.wireOp",EDGE,"E4.34.1");var subQ7=sQuery(id+"F2.wireOp",EDGE,"E1");var subQ8=makeQuery(id+"F2.imprint","INTERSECT",VERTEX,{"derivedFrom":[subQ7,subQ5]});Q191=makeQuery(id+"F2.imprint","IMPRINT",FACE,{"disambiguationData":[TD([[makeQuery(id+"F2.imprint","IMPRINT",EDGE,{"disambiguationData":[TD([[subQ8,-1.0]])],"derivedFrom":subQ7}),-1.0]])]});}
            var Q192;
            {var subQ3=sQuery(id+"F2.wireOp",EDGE,"E4.36.1");var subQ7=sQuery(id+"F2.wireOp",EDGE,"E1");var subQ8=makeQuery(id+"F2.imprint","INTERSECT",VERTEX,{"derivedFrom":[subQ7,subQ3]});Q192=makeQuery(id+"F2.imprint","IMPRINT",FACE,{"disambiguationData":[TD([[makeQuery(id+"F2.imprint","IMPRINT",EDGE,{"disambiguationData":[TD([[subQ8,-1.0]])],"derivedFrom":subQ7}),-1.0]])]});}
            var Q193;
            {var subQ5=sQuery(id+"F2.wireOp",EDGE,"E4.37.1");var subQ7=sQuery(id+"F2.wireOp",EDGE,"E1");var subQ8=makeQuery(id+"F2.imprint","INTERSECT",VERTEX,{"derivedFrom":[subQ7,subQ5]});Q193=makeQuery(id+"F2.imprint","IMPRINT",FACE,{"disambiguationData":[TD([[makeQuery(id+"F2.imprint","IMPRINT",EDGE,{"disambiguationData":[TD([[subQ8,-1.0]])],"derivedFrom":subQ7}),-1.0]])]});}
            var Q194;
            {var subQ3=sQuery(id+"F2.wireOp",EDGE,"E4.38.1");var subQ5=sQuery(id+"F2.wireOp",EDGE,"E1");var subQ6=makeQuery(id+"F2.imprint","INTERSECT",VERTEX,{"derivedFrom":[subQ5,subQ3]});Q194=makeQuery(id+"F2.imprint","IMPRINT",FACE,{"disambiguationData":[TD([[makeQuery(id+"F2.imprint","IMPRINT",EDGE,{"disambiguationData":[TD([[subQ6,-1.0]])],"derivedFrom":subQ5}),-1.0]])]});}
            var Q195;
            {var subQ5=sQuery(id+"F2.wireOp",EDGE,"E4.39.1");var subQ7=sQuery(id+"F2.wireOp",EDGE,"E1");var subQ8=makeQuery(id+"F2.imprint","INTERSECT",VERTEX,{"derivedFrom":[subQ7,subQ5]});Q195=makeQuery(id+"F2.imprint","IMPRINT",FACE,{"disambiguationData":[TD([[makeQuery(id+"F2.imprint","IMPRINT",EDGE,{"disambiguationData":[TD([[subQ8,-1.0]])],"derivedFrom":subQ7}),-1.0]])]});}
            var Q196;
            {var subQ5=sQuery(id+"F2.wireOp",EDGE,"E4.83.1");var subQ7=sQuery(id+"F2.wireOp",EDGE,"E1");var subQ8=makeQuery(id+"F2.imprint","INTERSECT",VERTEX,{"derivedFrom":[subQ7,subQ5]});Q196=makeQuery(id+"F2.imprint","IMPRINT",FACE,{"disambiguationData":[TD([[makeQuery(id+"F2.imprint","IMPRINT",EDGE,{"disambiguationData":[TD([[subQ8,-1.0]])],"derivedFrom":subQ7}),-1.0]])]});}
            var Q197;
            {var subQ5=sQuery(id+"F2.wireOp",EDGE,"E4.82.1");var subQ7=sQuery(id+"F2.wireOp",EDGE,"E1");var subQ8=makeQuery(id+"F2.imprint","INTERSECT",VERTEX,{"derivedFrom":[subQ7,subQ5]});Q197=makeQuery(id+"F2.imprint","IMPRINT",FACE,{"disambiguationData":[TD([[makeQuery(id+"F2.imprint","IMPRINT",EDGE,{"disambiguationData":[TD([[subQ8,-1.0]])],"derivedFrom":subQ7}),-1.0]])]});}
            var Q198;
            {var subQ3=sQuery(id+"F2.wireOp",EDGE,"E4.69.1");var subQ7=sQuery(id+"F2.wireOp",EDGE,"E1");var subQ8=makeQuery(id+"F2.imprint","INTERSECT",VERTEX,{"derivedFrom":[subQ7,subQ3]});Q198=makeQuery(id+"F2.imprint","IMPRINT",FACE,{"disambiguationData":[TD([[makeQuery(id+"F2.imprint","IMPRINT",EDGE,{"disambiguationData":[TD([[subQ8,-1.0]])],"derivedFrom":subQ7}),-1.0]])]});}
            var Q199;
            {var subQ5=sQuery(id+"F2.wireOp",EDGE,"E4.57.1");var subQ7=sQuery(id+"F2.wireOp",EDGE,"E1");var subQ8=makeQuery(id+"F2.imprint","INTERSECT",VERTEX,{"derivedFrom":[subQ7,subQ5]});Q199=makeQuery(id+"F2.imprint","IMPRINT",FACE,{"disambiguationData":[TD([[makeQuery(id+"F2.imprint","IMPRINT",EDGE,{"disambiguationData":[TD([[subQ8,-1.0]])],"derivedFrom":subQ7}),-1.0]])]});}
            var Q200;
            {var subQ5=sQuery(id+"F2.wireOp",EDGE,"E4.63.1");var subQ6=sQuery(id+"F2.wireOp",EDGE,"E1");var subQ7=makeQuery(id+"F2.imprint","INTERSECT",VERTEX,{"derivedFrom":[subQ6,subQ5]});Q200=makeQuery(id+"F2.imprint","IMPRINT",FACE,{"disambiguationData":[TD([[makeQuery(id+"F2.imprint","IMPRINT",EDGE,{"disambiguationData":[TD([[subQ7,-1.0]])],"derivedFrom":subQ6}),-1.0]])]});}
            var Q201;
            {var subQ5=sQuery(id+"F2.wireOp",EDGE,"E4.62.1");var subQ7=sQuery(id+"F2.wireOp",EDGE,"E1");var subQ8=makeQuery(id+"F2.imprint","INTERSECT",VERTEX,{"derivedFrom":[subQ7,subQ5]});Q201=makeQuery(id+"F2.imprint","IMPRINT",FACE,{"disambiguationData":[TD([[makeQuery(id+"F2.imprint","IMPRINT",EDGE,{"disambiguationData":[TD([[subQ8,-1.0]])],"derivedFrom":subQ7}),-1.0]])]});}
            var Q202;
            {var subQ3=sQuery(id+"F2.wireOp",EDGE,"E4.58.1");var subQ5=sQuery(id+"F2.wireOp",EDGE,"E1");var subQ6=makeQuery(id+"F2.imprint","INTERSECT",VERTEX,{"derivedFrom":[subQ5,subQ3]});Q202=makeQuery(id+"F2.imprint","IMPRINT",FACE,{"disambiguationData":[TD([[makeQuery(id+"F2.imprint","IMPRINT",EDGE,{"disambiguationData":[TD([[subQ6,-1.0]])],"derivedFrom":subQ5}),-1.0]])]});}
            var Q203;
            {var subQ3=sQuery(id+"F2.wireOp",EDGE,"E5.3.86.0");var subQ5=sQuery(id+"F2.wireOp",EDGE,"E1");var subQ6=makeQuery(id+"F2.imprint","INTERSECT",VERTEX,{"derivedFrom":[subQ5,subQ3]});Q203=makeQuery(id+"F2.imprint","IMPRINT",FACE,{"disambiguationData":[TD([[makeQuery(id+"F2.imprint","IMPRINT",EDGE,{"disambiguationData":[TD([[subQ6,-1.0]])],"derivedFrom":subQ5}),-1.0]])]});}
            var Q204;
            {var subQ5=sQuery(id+"F2.wireOp",EDGE,"E5.3.87.0");var subQ7=sQuery(id+"F2.wireOp",EDGE,"E1");var subQ8=makeQuery(id+"F2.imprint","INTERSECT",VERTEX,{"derivedFrom":[subQ7,subQ5]});Q204=makeQuery(id+"F2.imprint","IMPRINT",FACE,{"disambiguationData":[TD([[makeQuery(id+"F2.imprint","IMPRINT",EDGE,{"disambiguationData":[TD([[subQ8,-1.0]])],"derivedFrom":subQ7}),-1.0]])]});}
            var Q205;
            {var subQ3=sQuery(id+"F2.wireOp",EDGE,"E5.3.88.0");var subQ6=sQuery(id+"F2.wireOp",EDGE,"E1");var subQ9=makeQuery(id+"F2.imprint","INTERSECT",VERTEX,{"derivedFrom":[subQ6,subQ3]});Q205=makeQuery(id+"F2.imprint","IMPRINT",FACE,{"disambiguationData":[TD([[makeQuery(id+"F2.imprint","IMPRINT",EDGE,{"disambiguationData":[TD([[subQ9,-1.0]])],"derivedFrom":subQ6}),-1.0]])]});}
            var Q206;
            {var subQ5=sQuery(id+"F2.wireOp",EDGE,"E6.3.112.0");var subQ7=sQuery(id+"F2.wireOp",EDGE,"E1");var subQ8=makeQuery(id+"F2.imprint","INTERSECT",VERTEX,{"derivedFrom":[subQ7,subQ5]});Q206=makeQuery(id+"F2.imprint","IMPRINT",FACE,{"disambiguationData":[TD([[makeQuery(id+"F2.imprint","IMPRINT",EDGE,{"disambiguationData":[TD([[subQ8,-1.0]])],"derivedFrom":subQ7}),-1.0]])]});}
            var Q207;
            {var subQ5=sQuery(id+"F2.wireOp",EDGE,"E6.3.104.0");var subQ7=sQuery(id+"F2.wireOp",EDGE,"E1");var subQ8=makeQuery(id+"F2.imprint","INTERSECT",VERTEX,{"derivedFrom":[subQ7,subQ5]});Q207=makeQuery(id+"F2.imprint","IMPRINT",FACE,{"disambiguationData":[TD([[makeQuery(id+"F2.imprint","IMPRINT",EDGE,{"disambiguationData":[TD([[subQ8,-1.0]])],"derivedFrom":subQ7}),-1.0]])]});}
            var Q208;
            {var subQ5=sQuery(id+"F2.wireOp",EDGE,"E5.3.96.0");var subQ6=sQuery(id+"F2.wireOp",EDGE,"E1");var subQ7=makeQuery(id+"F2.imprint","INTERSECT",VERTEX,{"derivedFrom":[subQ6,subQ5]});Q208=makeQuery(id+"F2.imprint","IMPRINT",FACE,{"disambiguationData":[TD([[makeQuery(id+"F2.imprint","IMPRINT",EDGE,{"disambiguationData":[TD([[subQ7,-1.0]])],"derivedFrom":subQ6}),-1.0]])]});}
            var Q209;
            {var subQ5=sQuery(id+"F2.wireOp",EDGE,"E5.3.85.0");var subQ7=sQuery(id+"F2.wireOp",EDGE,"E1");var subQ8=makeQuery(id+"F2.imprint","INTERSECT",VERTEX,{"derivedFrom":[subQ7,subQ5]});Q209=makeQuery(id+"F2.imprint","IMPRINT",FACE,{"disambiguationData":[TD([[makeQuery(id+"F2.imprint","IMPRINT",EDGE,{"disambiguationData":[TD([[subQ8,-1.0]])],"derivedFrom":subQ7}),-1.0]])]});}
            var Q210;
            {var subQ5=sQuery(id+"F2.wireOp",EDGE,"E6.3.105.0");var subQ7=sQuery(id+"F2.wireOp",EDGE,"E1");var subQ8=makeQuery(id+"F2.imprint","INTERSECT",VERTEX,{"derivedFrom":[subQ7,subQ5]});Q210=makeQuery(id+"F2.imprint","IMPRINT",FACE,{"disambiguationData":[TD([[makeQuery(id+"F2.imprint","IMPRINT",EDGE,{"disambiguationData":[TD([[subQ8,-1.0]])],"derivedFrom":subQ7}),-1.0]])]});}
            var Q211;
            {var subQ5=sQuery(id+"F2.wireOp",EDGE,"E5.3.97.0");var subQ7=sQuery(id+"F2.wireOp",EDGE,"E1");var subQ8=makeQuery(id+"F2.imprint","INTERSECT",VERTEX,{"derivedFrom":[subQ7,subQ5]});Q211=makeQuery(id+"F2.imprint","IMPRINT",FACE,{"disambiguationData":[TD([[makeQuery(id+"F2.imprint","IMPRINT",EDGE,{"disambiguationData":[TD([[subQ8,-1.0]])],"derivedFrom":subQ7}),-1.0]])]});}
            var Q212;
            {var subQ5=sQuery(id+"F2.wireOp",EDGE,"E6.3.106.0");var subQ7=sQuery(id+"F2.wireOp",EDGE,"E1");var subQ8=makeQuery(id+"F2.imprint","INTERSECT",VERTEX,{"derivedFrom":[subQ7,subQ5]});Q212=makeQuery(id+"F2.imprint","IMPRINT",FACE,{"disambiguationData":[TD([[makeQuery(id+"F2.imprint","IMPRINT",EDGE,{"disambiguationData":[TD([[subQ8,-1.0]])],"derivedFrom":subQ7}),-1.0]])]});}
            var Q213;
            {var subQ5=sQuery(id+"F2.wireOp",EDGE,"E5.3.98.0");var subQ7=sQuery(id+"F2.wireOp",EDGE,"E1");var subQ8=makeQuery(id+"F2.imprint","INTERSECT",VERTEX,{"derivedFrom":[subQ7,subQ5]});Q213=makeQuery(id+"F2.imprint","IMPRINT",FACE,{"disambiguationData":[TD([[makeQuery(id+"F2.imprint","IMPRINT",EDGE,{"disambiguationData":[TD([[subQ8,-1.0]])],"derivedFrom":subQ7}),-1.0]])]});}
            var Q214;
            {var subQ5=sQuery(id+"F2.wireOp",EDGE,"E6.3.100.0");var subQ6=sQuery(id+"F2.wireOp",EDGE,"E1");var subQ7=makeQuery(id+"F2.imprint","INTERSECT",VERTEX,{"derivedFrom":[subQ6,subQ5]});Q214=makeQuery(id+"F2.imprint","IMPRINT",FACE,{"disambiguationData":[TD([[makeQuery(id+"F2.imprint","IMPRINT",EDGE,{"disambiguationData":[TD([[subQ7,-1.0]])],"derivedFrom":subQ6}),-1.0]])]});}
            var Q215;
            {var subQ5=sQuery(id+"F2.wireOp",EDGE,"E6.3.108.0");var subQ7=sQuery(id+"F2.wireOp",EDGE,"E1");var subQ8=makeQuery(id+"F2.imprint","INTERSECT",VERTEX,{"derivedFrom":[subQ7,subQ5]});Q215=makeQuery(id+"F2.imprint","IMPRINT",FACE,{"disambiguationData":[TD([[makeQuery(id+"F2.imprint","IMPRINT",EDGE,{"disambiguationData":[TD([[subQ8,-1.0]])],"derivedFrom":subQ7}),-1.0]])]});}
            var Q216;
            {var subQ5=sQuery(id+"F2.wireOp",EDGE,"E6.3.107.0");var subQ7=sQuery(id+"F2.wireOp",EDGE,"E1");var subQ8=makeQuery(id+"F2.imprint","INTERSECT",VERTEX,{"derivedFrom":[subQ7,subQ5]});Q216=makeQuery(id+"F2.imprint","IMPRINT",FACE,{"disambiguationData":[TD([[makeQuery(id+"F2.imprint","IMPRINT",EDGE,{"disambiguationData":[TD([[subQ8,-1.0]])],"derivedFrom":subQ7}),-1.0]])]});}
            var Q217;
            {var subQ5=sQuery(id+"F2.wireOp",EDGE,"E5.3.99.0");var subQ7=sQuery(id+"F2.wireOp",EDGE,"E1");var subQ8=makeQuery(id+"F2.imprint","INTERSECT",VERTEX,{"derivedFrom":[subQ7,subQ5]});Q217=makeQuery(id+"F2.imprint","IMPRINT",FACE,{"disambiguationData":[TD([[makeQuery(id+"F2.imprint","IMPRINT",EDGE,{"disambiguationData":[TD([[subQ8,-1.0]])],"derivedFrom":subQ7}),-1.0]])]});}
            var Q218;
            {var subQ5=sQuery(id+"F2.wireOp",EDGE,"E6.3.101.0");var subQ7=sQuery(id+"F2.wireOp",EDGE,"E1");var subQ8=makeQuery(id+"F2.imprint","INTERSECT",VERTEX,{"derivedFrom":[subQ7,subQ5]});Q218=makeQuery(id+"F2.imprint","IMPRINT",FACE,{"disambiguationData":[TD([[makeQuery(id+"F2.imprint","IMPRINT",EDGE,{"disambiguationData":[TD([[subQ8,-1.0]])],"derivedFrom":subQ7}),-1.0]])]});}
            var Q219;
            {var subQ5=sQuery(id+"F2.wireOp",EDGE,"E5.3.93.0");var subQ7=sQuery(id+"F2.wireOp",EDGE,"E1");var subQ8=makeQuery(id+"F2.imprint","INTERSECT",VERTEX,{"derivedFrom":[subQ7,subQ5]});Q219=makeQuery(id+"F2.imprint","IMPRINT",FACE,{"disambiguationData":[TD([[makeQuery(id+"F2.imprint","IMPRINT",EDGE,{"disambiguationData":[TD([[subQ8,-1.0]])],"derivedFrom":subQ7}),-1.0]])]});}
            var Q220;
            {var subQ5=sQuery(id+"F2.wireOp",EDGE,"E6.3.109.0");var subQ7=sQuery(id+"F2.wireOp",EDGE,"E1");var subQ8=makeQuery(id+"F2.imprint","INTERSECT",VERTEX,{"derivedFrom":[subQ7,subQ5]});Q220=makeQuery(id+"F2.imprint","IMPRINT",FACE,{"disambiguationData":[TD([[makeQuery(id+"F2.imprint","IMPRINT",EDGE,{"disambiguationData":[TD([[subQ8,-1.0]])],"derivedFrom":subQ7}),-1.0]])]});}
            var Q221;
            {var subQ5=sQuery(id+"F2.wireOp",EDGE,"E6.3.102.0");var subQ7=sQuery(id+"F2.wireOp",EDGE,"E1");var subQ8=makeQuery(id+"F2.imprint","INTERSECT",VERTEX,{"derivedFrom":[subQ7,subQ5]});Q221=makeQuery(id+"F2.imprint","IMPRINT",FACE,{"disambiguationData":[TD([[makeQuery(id+"F2.imprint","IMPRINT",EDGE,{"disambiguationData":[TD([[subQ8,-1.0]])],"derivedFrom":subQ7}),-1.0]])]});}
            var Q222;
            {var subQ5=sQuery(id+"F2.wireOp",EDGE,"E5.3.94.0");var subQ7=sQuery(id+"F2.wireOp",EDGE,"E1");var subQ8=makeQuery(id+"F2.imprint","INTERSECT",VERTEX,{"derivedFrom":[subQ7,subQ5]});Q222=makeQuery(id+"F2.imprint","IMPRINT",FACE,{"disambiguationData":[TD([[makeQuery(id+"F2.imprint","IMPRINT",EDGE,{"disambiguationData":[TD([[subQ8,-1.0]])],"derivedFrom":subQ7}),-1.0]])]});}
            var Q223;
            {var subQ5=sQuery(id+"F2.wireOp",EDGE,"E6.3.110.0");var subQ7=sQuery(id+"F2.wireOp",EDGE,"E1");var subQ9=makeQuery(id+"F2.imprint","INTERSECT",VERTEX,{"derivedFrom":[subQ7,subQ5]});Q223=makeQuery(id+"F2.imprint","IMPRINT",FACE,{"disambiguationData":[TD([[makeQuery(id+"F2.imprint","IMPRINT",EDGE,{"disambiguationData":[TD([[subQ9,-1.0]])],"derivedFrom":subQ7}),-1.0]])]});}
            var Q224;
            {var subQ3=sQuery(id+"F2.wireOp",EDGE,"E5.3.92.0");var subQ7=sQuery(id+"F2.wireOp",EDGE,"E1");var subQ8=makeQuery(id+"F2.imprint","INTERSECT",VERTEX,{"derivedFrom":[subQ7,subQ3]});Q224=makeQuery(id+"F2.imprint","IMPRINT",FACE,{"disambiguationData":[TD([[makeQuery(id+"F2.imprint","IMPRINT",EDGE,{"disambiguationData":[TD([[subQ8,-1.0]])],"derivedFrom":subQ7}),-1.0]])]});}
            var Q225;
            {var subQ5=sQuery(id+"F2.wireOp",EDGE,"E5.3.89.0");var subQ7=sQuery(id+"F2.wireOp",EDGE,"E1");var subQ8=makeQuery(id+"F2.imprint","INTERSECT",VERTEX,{"derivedFrom":[subQ7,subQ5]});Q225=makeQuery(id+"F2.imprint","IMPRINT",FACE,{"disambiguationData":[TD([[makeQuery(id+"F2.imprint","IMPRINT",EDGE,{"disambiguationData":[TD([[subQ8,-1.0]])],"derivedFrom":subQ7}),-1.0]])]});}
            var Q226;
            {var subQ5=sQuery(id+"F2.wireOp",EDGE,"E5.3.90.0");var subQ7=sQuery(id+"F2.wireOp",EDGE,"E1");var subQ8=makeQuery(id+"F2.imprint","INTERSECT",VERTEX,{"derivedFrom":[subQ7,subQ5]});Q226=makeQuery(id+"F2.imprint","IMPRINT",FACE,{"disambiguationData":[TD([[makeQuery(id+"F2.imprint","IMPRINT",EDGE,{"disambiguationData":[TD([[subQ8,-1.0]])],"derivedFrom":subQ7}),-1.0]])]});}
            var Q227;
            {var subQ5=sQuery(id+"F2.wireOp",EDGE,"E5.3.91.0");var subQ7=sQuery(id+"F2.wireOp",EDGE,"E1");var subQ8=makeQuery(id+"F2.imprint","INTERSECT",VERTEX,{"derivedFrom":[subQ7,subQ5]});Q227=makeQuery(id+"F2.imprint","IMPRINT",FACE,{"disambiguationData":[TD([[makeQuery(id+"F2.imprint","IMPRINT",EDGE,{"disambiguationData":[TD([[subQ8,-1.0]])],"derivedFrom":subQ7}),-1.0]])]});}
            var Q228;
            {var subQ5=sQuery(id+"F2.wireOp",EDGE,"E6.3.103.0");var subQ7=sQuery(id+"F2.wireOp",EDGE,"E1");var subQ8=makeQuery(id+"F2.imprint","INTERSECT",VERTEX,{"derivedFrom":[subQ7,subQ5]});Q228=makeQuery(id+"F2.imprint","IMPRINT",FACE,{"disambiguationData":[TD([[makeQuery(id+"F2.imprint","IMPRINT",EDGE,{"disambiguationData":[TD([[subQ8,-1.0]])],"derivedFrom":subQ7}),-1.0]])]});}
            var Q229;
            {var subQ5=sQuery(id+"F2.wireOp",EDGE,"E5.3.95.0");var subQ7=sQuery(id+"F2.wireOp",EDGE,"E1");var subQ8=makeQuery(id+"F2.imprint","INTERSECT",VERTEX,{"derivedFrom":[subQ7,subQ5]});Q229=makeQuery(id+"F2.imprint","IMPRINT",FACE,{"disambiguationData":[TD([[makeQuery(id+"F2.imprint","IMPRINT",EDGE,{"disambiguationData":[TD([[subQ8,-1.0]])],"derivedFrom":subQ7}),-1.0]])]});}
            var Q230;
            {var subQ5=sQuery(id+"F2.wireOp",EDGE,"E6.3.111.0");var subQ6=sQuery(id+"F2.wireOp",EDGE,"E1");var subQ7=makeQuery(id+"F2.imprint","INTERSECT",VERTEX,{"derivedFrom":[subQ6,subQ5]});Q230=makeQuery(id+"F2.imprint","IMPRINT",FACE,{"disambiguationData":[TD([[makeQuery(id+"F2.imprint","IMPRINT",EDGE,{"disambiguationData":[TD([[subQ7,-1.0]])],"derivedFrom":subQ6}),-1.0]])]});}
            var Q231;
            Q231=makeQuery(id+"F2.imprint","IMPRINT",FACE,{"disambiguationData":[TD([[makeQuery(id+"F2.imprint","IMPRINT",EDGE,{"derivedFrom":makeQuery(id+"F1.opExtrude","CAP_EDGE",EDGE,{"disambiguationData":[OSD([sQuery(id+"F0.wireOp",EDGE,"E0")])],"isStart":false})}),1.0]])]});
            extrude(context, id + "F3", {"entities" : qUnion([Q0, Q1, Q2, Q3, Q4, Q5, Q6, Q7, Q8, Q9, Q10, Q11, Q12, Q13, Q14, Q15, Q16, Q17, Q18, Q19, Q20, Q21, Q22, Q23, Q24, Q25, Q26, Q27, Q28, Q29, Q30, Q31, Q32, Q33, Q34, Q35, Q36, Q37, Q38, Q39, Q40, Q41, Q42, Q43, Q44, Q45, Q46, Q47, Q48, Q49, Q50, Q51, Q52, Q53, Q54, Q55, Q56, Q57, Q58, Q59, Q60, Q61, Q62, Q63, Q64, Q65, Q66, Q67, Q68, Q69, Q70, Q71, Q72, Q73, Q74, Q75, Q76, Q77, Q78, Q79, Q80, Q81, Q82, Q83, Q84, Q85, Q86, Q87, Q88, Q89, Q90, Q91, Q92, Q93, Q94, Q95, Q96, Q97, Q98, Q99, Q100, Q101, Q102, Q103, Q104, Q105, Q106, Q107, Q108, Q109, Q110, Q111, Q112, Q113, Q114, Q115, Q116, Q117, Q118, Q119, Q120, Q121, Q122, Q123, Q124, Q125, Q126, Q127, Q128, Q129, Q130, Q131, Q132, Q133, Q134, Q135, Q136, Q137, Q138, Q139, Q140, Q141, Q142, Q143, Q144, Q145, Q146, Q147, Q148, Q149, Q150, Q151, Q152, Q153, Q154, Q155, Q156, Q157, Q158, Q159, Q160, Q161, Q162, Q163, Q164, Q165, Q166, Q167, Q168, Q169, Q170, Q171, Q172, Q173, Q174, Q175, Q176, Q177, Q178, Q179, Q180, Q181, Q182, Q183, Q184, Q185, Q186, Q187, Q188, Q189, Q190, Q191, Q192, Q193, Q194, Q195, Q196, Q197, Q198, Q199, Q200, Q201, Q202, Q203, Q204, Q205, Q206, Q207, Q208, Q209, Q210, Q211, Q212, Q213, Q214, Q215, Q216, Q217, Q218, Q219, Q220, Q221, Q222, Q223, Q224, Q225, Q226, Q227, Q228, Q229, Q230, Q231]), "depth" : 3 * mm});
        }
        {
            var Q0;
            Q0=makeQuery(id+"F1.opExtrude","CAP_FACE",FACE,{"disambiguationData":[OSD([sQuery(id+"F0.wireOp",EDGE,"E0")])],"isStart":true});
            extrude(context, id + "F4", {"entities" : qUnion([Q0]), "operationType" : NewBodyOperationType.REMOVE, "oppositeDirection" : true, "depth" : 3 * mm});
        }
        {
            var Q0;
            Q0=makeQuery(id+"F3.opExtrude","CAP_FACE",FACE,{"disambiguationData":[OSD([sQuery(id+"F2.wireOp",EDGE,"E2"),sQuery(id+"F2.wireOp",EDGE,"E3"),sQuery(id+"F2.wireOp",EDGE,"E4.1.0"),sQuery(id+"F2.wireOp",EDGE,"E4.1.1"),sQuery(id+"F2.wireOp",EDGE,"E4.2.0"),sQuery(id+"F2.wireOp",EDGE,"E4.2.1"),sQuery(id+"F2.wireOp",EDGE,"E4.3.0"),sQuery(id+"F2.wireOp",EDGE,"E4.3.1"),sQuery(id+"F2.wireOp",EDGE,"E4.4.0"),sQuery(id+"F2.wireOp",EDGE,"E4.4.1"),sQuery(id+"F2.wireOp",EDGE,"E4.5.0"),sQuery(id+"F2.wireOp",EDGE,"E4.5.1"),sQuery(id+"F2.wireOp",EDGE,"E4.6.0"),sQuery(id+"F2.wireOp",EDGE,"E4.6.1"),sQuery(id+"F2.wireOp",EDGE,"E4.7.0"),sQuery(id+"F2.wireOp",EDGE,"E4.7.1"),sQuery(id+"F2.wireOp",EDGE,"E4.8.0"),sQuery(id+"F2.wireOp",EDGE,"E4.8.1"),sQuery(id+"F2.wireOp",EDGE,"E4.9.0"),sQuery(id+"F2.wireOp",EDGE,"E4.9.1"),sQuery(id+"F2.wireOp",EDGE,"E4.10.0"),sQuery(id+"F2.wireOp",EDGE,"E4.10.1"),sQuery(id+"F2.wireOp",EDGE,"E4.11.0"),sQuery(id+"F2.wireOp",EDGE,"E4.11.1"),sQuery(id+"F2.wireOp",EDGE,"E4.12.0"),sQuery(id+"F2.wireOp",EDGE,"E4.12.1"),sQuery(id+"F2.wireOp",EDGE,"E4.13.0"),sQuery(id+"F2.wireOp",EDGE,"E4.13.1"),sQuery(id+"F2.wireOp",EDGE,"E4.14.0"),sQuery(id+"F2.wireOp",EDGE,"E4.14.1"),sQuery(id+"F2.wireOp",EDGE,"E4.15.0"),sQuery(id+"F2.wireOp",EDGE,"E4.15.1"),sQuery(id+"F2.wireOp",EDGE,"E4.16.0"),sQuery(id+"F2.wireOp",EDGE,"E4.16.1"),sQuery(id+"F2.wireOp",EDGE,"E4.17.0"),sQuery(id+"F2.wireOp",EDGE,"E4.17.1"),sQuery(id+"F2.wireOp",EDGE,"E4.18.0"),sQuery(id+"F2.wireOp",EDGE,"E4.18.1"),sQuery(id+"F2.wireOp",EDGE,"E4.19.0"),sQuery(id+"F2.wireOp",EDGE,"E4.19.1"),sQuery(id+"F2.wireOp",EDGE,"E4.20.0"),sQuery(id+"F2.wireOp",EDGE,"E4.20.1"),sQuery(id+"F2.wireOp",EDGE,"E4.21.0"),sQuery(id+"F2.wireOp",EDGE,"E4.21.1"),sQuery(id+"F2.wireOp",EDGE,"E4.22.0"),sQuery(id+"F2.wireOp",EDGE,"E4.22.1"),sQuery(id+"F2.wireOp",EDGE,"E4.23.0"),sQuery(id+"F2.wireOp",EDGE,"E4.23.1"),sQuery(id+"F2.wireOp",EDGE,"E4.24.0"),sQuery(id+"F2.wireOp",EDGE,"E4.24.1"),sQuery(id+"F2.wireOp",EDGE,"E4.25.0"),sQuery(id+"F2.wireOp",EDGE,"E4.25.1"),sQuery(id+"F2.wireOp",EDGE,"E4.26.0"),sQuery(id+"F2.wireOp",EDGE,"E4.26.1"),sQuery(id+"F2.wireOp",EDGE,"E4.27.0"),sQuery(id+"F2.wireOp",EDGE,"E4.27.1"),sQuery(id+"F2.wireOp",EDGE,"E4.28.0"),sQuery(id+"F2.wireOp",EDGE,"E4.28.1"),sQuery(id+"F2.wireOp",EDGE,"E4.29.0"),sQuery(id+"F2.wireOp",EDGE,"E4.29.1"),sQuery(id+"F2.wireOp",EDGE,"E4.30.0"),sQuery(id+"F2.wireOp",EDGE,"E4.30.1"),sQuery(id+"F2.wireOp",EDGE,"E4.31.0"),sQuery(id+"F2.wireOp",EDGE,"E4.31.1"),sQuery(id+"F2.wireOp",EDGE,"E4.32.0"),sQuery(id+"F2.wireOp",EDGE,"E4.32.1"),sQuery(id+"F2.wireOp",EDGE,"E4.33.0"),sQuery(id+"F2.wireOp",EDGE,"E4.33.1"),sQuery(id+"F2.wireOp",EDGE,"E4.34.0"),sQuery(id+"F2.wireOp",EDGE,"E4.34.1"),sQuery(id+"F2.wireOp",EDGE,"E4.35.0"),sQuery(id+"F2.wireOp",EDGE,"E4.35.1"),sQuery(id+"F2.wireOp",EDGE,"E4.36.0"),sQuery(id+"F2.wireOp",EDGE,"E4.36.1"),sQuery(id+"F2.wireOp",EDGE,"E4.37.0"),sQuery(id+"F2.wireOp",EDGE,"E4.37.1"),sQuery(id+"F2.wireOp",EDGE,"E4.38.0"),sQuery(id+"F2.wireOp",EDGE,"E4.38.1"),sQuery(id+"F2.wireOp",EDGE,"E4.39.0"),sQuery(id+"F2.wireOp",EDGE,"E4.39.1"),sQuery(id+"F2.wireOp",EDGE,"E4.40.0"),sQuery(id+"F2.wireOp",EDGE,"E4.40.1"),sQuery(id+"F2.wireOp",EDGE,"E4.41.0"),sQuery(id+"F2.wireOp",EDGE,"E4.41.1"),sQuery(id+"F2.wireOp",EDGE,"E4.42.0"),sQuery(id+"F2.wireOp",EDGE,"E4.42.1"),sQuery(id+"F2.wireOp",EDGE,"E4.43.0"),sQuery(id+"F2.wireOp",EDGE,"E4.43.1"),sQuery(id+"F2.wireOp",EDGE,"E4.44.0"),sQuery(id+"F2.wireOp",EDGE,"E4.44.1"),sQuery(id+"F2.wireOp",EDGE,"E4.45.0"),sQuery(id+"F2.wireOp",EDGE,"E4.45.1"),sQuery(id+"F2.wireOp",EDGE,"E4.46.0"),sQuery(id+"F2.wireOp",EDGE,"E4.46.1"),sQuery(id+"F2.wireOp",EDGE,"E4.47.0"),sQuery(id+"F2.wireOp",EDGE,"E4.47.1"),sQuery(id+"F2.wireOp",EDGE,"E4.48.0"),sQuery(id+"F2.wireOp",EDGE,"E4.48.1"),sQuery(id+"F2.wireOp",EDGE,"E4.49.0"),sQuery(id+"F2.wireOp",EDGE,"E4.49.1"),sQuery(id+"F2.wireOp",EDGE,"E4.50.0"),sQuery(id+"F2.wireOp",EDGE,"E4.50.1"),sQuery(id+"F2.wireOp",EDGE,"E4.51.0"),sQuery(id+"F2.wireOp",EDGE,"E4.51.1"),sQuery(id+"F2.wireOp",EDGE,"E4.52.0"),sQuery(id+"F2.wireOp",EDGE,"E4.52.1"),sQuery(id+"F2.wireOp",EDGE,"E4.53.0"),sQuery(id+"F2.wireOp",EDGE,"E4.53.1"),sQuery(id+"F2.wireOp",EDGE,"E4.54.0"),sQuery(id+"F2.wireOp",EDGE,"E4.54.1"),sQuery(id+"F2.wireOp",EDGE,"E4.55.0"),sQuery(id+"F2.wireOp",EDGE,"E4.55.1"),sQuery(id+"F2.wireOp",EDGE,"E4.56.0"),sQuery(id+"F2.wireOp",EDGE,"E4.56.1"),sQuery(id+"F2.wireOp",EDGE,"E4.57.0"),sQuery(id+"F2.wireOp",EDGE,"E4.57.1"),sQuery(id+"F2.wireOp",EDGE,"E4.58.0"),sQuery(id+"F2.wireOp",EDGE,"E4.58.1"),sQuery(id+"F2.wireOp",EDGE,"E4.59.0"),sQuery(id+"F2.wireOp",EDGE,"E4.59.1"),sQuery(id+"F2.wireOp",EDGE,"E4.60.0"),sQuery(id+"F2.wireOp",EDGE,"E4.60.1"),sQuery(id+"F2.wireOp",EDGE,"E4.61.0"),sQuery(id+"F2.wireOp",EDGE,"E4.61.1"),sQuery(id+"F2.wireOp",EDGE,"E4.62.0"),sQuery(id+"F2.wireOp",EDGE,"E4.62.1"),sQuery(id+"F2.wireOp",EDGE,"E4.63.0"),sQuery(id+"F2.wireOp",EDGE,"E4.63.1"),sQuery(id+"F2.wireOp",EDGE,"E4.64.0"),sQuery(id+"F2.wireOp",EDGE,"E4.64.1"),sQuery(id+"F2.wireOp",EDGE,"E4.65.0"),sQuery(id+"F2.wireOp",EDGE,"E4.65.1"),sQuery(id+"F2.wireOp",EDGE,"E4.66.0"),sQuery(id+"F2.wireOp",EDGE,"E4.66.1"),sQuery(id+"F2.wireOp",EDGE,"E4.67.0"),sQuery(id+"F2.wireOp",EDGE,"E4.67.1"),sQuery(id+"F2.wireOp",EDGE,"E4.68.0"),sQuery(id+"F2.wireOp",EDGE,"E4.68.1"),sQuery(id+"F2.wireOp",EDGE,"E4.69.0"),sQuery(id+"F2.wireOp",EDGE,"E4.69.1"),sQuery(id+"F2.wireOp",EDGE,"E4.70.0"),sQuery(id+"F2.wireOp",EDGE,"E4.70.1"),sQuery(id+"F2.wireOp",EDGE,"E4.71.0"),sQuery(id+"F2.wireOp",EDGE,"E4.71.1"),sQuery(id+"F2.wireOp",EDGE,"E4.72.0"),sQuery(id+"F2.wireOp",EDGE,"E4.72.1"),sQuery(id+"F2.wireOp",EDGE,"E4.73.0"),sQuery(id+"F2.wireOp",EDGE,"E4.73.1"),sQuery(id+"F2.wireOp",EDGE,"E4.74.0"),sQuery(id+"F2.wireOp",EDGE,"E4.74.1"),sQuery(id+"F2.wireOp",EDGE,"E4.75.0"),sQuery(id+"F2.wireOp",EDGE,"E4.75.1"),sQuery(id+"F2.wireOp",EDGE,"E4.76.0"),sQuery(id+"F2.wireOp",EDGE,"E4.76.1"),sQuery(id+"F2.wireOp",EDGE,"E4.77.0"),sQuery(id+"F2.wireOp",EDGE,"E4.77.1"),sQuery(id+"F2.wireOp",EDGE,"E4.78.0"),sQuery(id+"F2.wireOp",EDGE,"E4.78.1"),sQuery(id+"F2.wireOp",EDGE,"E4.79.0"),sQuery(id+"F2.wireOp",EDGE,"E4.79.1"),sQuery(id+"F2.wireOp",EDGE,"E4.80.0"),sQuery(id+"F2.wireOp",EDGE,"E4.80.1"),sQuery(id+"F2.wireOp",EDGE,"E4.81.0"),sQuery(id+"F2.wireOp",EDGE,"E4.81.1"),sQuery(id+"F2.wireOp",EDGE,"E4.82.0"),sQuery(id+"F2.wireOp",EDGE,"E4.82.1"),sQuery(id+"F2.wireOp",EDGE,"E4.83.0"),sQuery(id+"F2.wireOp",EDGE,"E4.83.1"),sQuery(id+"F2.wireOp",EDGE,"E4.84.0"),sQuery(id+"F2.wireOp",EDGE,"E4.84.1"),sQuery(id+"F2.wireOp",EDGE,"E5.2.85.0"),sQuery(id+"F2.wireOp",EDGE,"E5.3.85.0"),sQuery(id+"F2.wireOp",EDGE,"E5.2.86.0"),sQuery(id+"F2.wireOp",EDGE,"E5.3.86.0"),sQuery(id+"F2.wireOp",EDGE,"E5.2.87.0"),sQuery(id+"F2.wireOp",EDGE,"E5.3.87.0"),sQuery(id+"F2.wireOp",EDGE,"E5.2.88.0"),sQuery(id+"F2.wireOp",EDGE,"E5.3.88.0"),sQuery(id+"F2.wireOp",EDGE,"E5.2.89.0"),sQuery(id+"F2.wireOp",EDGE,"E5.3.89.0"),sQuery(id+"F2.wireOp",EDGE,"E5.2.90.0"),sQuery(id+"F2.wireOp",EDGE,"E5.3.90.0"),sQuery(id+"F2.wireOp",EDGE,"E5.2.91.0"),sQuery(id+"F2.wireOp",EDGE,"E5.3.91.0"),sQuery(id+"F2.wireOp",EDGE,"E5.2.92.0"),sQuery(id+"F2.wireOp",EDGE,"E5.3.92.0"),sQuery(id+"F2.wireOp",EDGE,"E5.2.93.0"),sQuery(id+"F2.wireOp",EDGE,"E5.3.93.0"),sQuery(id+"F2.wireOp",EDGE,"E5.2.94.0"),sQuery(id+"F2.wireOp",EDGE,"E5.3.94.0"),sQuery(id+"F2.wireOp",EDGE,"E5.2.95.0"),sQuery(id+"F2.wireOp",EDGE,"E5.3.95.0"),sQuery(id+"F2.wireOp",EDGE,"E5.2.96.0"),sQuery(id+"F2.wireOp",EDGE,"E5.3.96.0"),sQuery(id+"F2.wireOp",EDGE,"E5.2.97.0"),sQuery(id+"F2.wireOp",EDGE,"E5.3.97.0"),sQuery(id+"F2.wireOp",EDGE,"E5.2.98.0"),sQuery(id+"F2.wireOp",EDGE,"E5.3.98.0"),sQuery(id+"F2.wireOp",EDGE,"E5.2.99.0"),sQuery(id+"F2.wireOp",EDGE,"E5.3.99.0"),sQuery(id+"F2.wireOp",EDGE,"E6.2.100.0"),sQuery(id+"F2.wireOp",EDGE,"E6.3.100.0"),sQuery(id+"F2.wireOp",EDGE,"E6.2.101.0"),sQuery(id+"F2.wireOp",EDGE,"E6.3.101.0"),sQuery(id+"F2.wireOp",EDGE,"E6.2.102.0"),sQuery(id+"F2.wireOp",EDGE,"E6.3.102.0"),sQuery(id+"F2.wireOp",EDGE,"E6.2.103.0"),sQuery(id+"F2.wireOp",EDGE,"E6.3.103.0"),sQuery(id+"F2.wireOp",EDGE,"E6.2.104.0"),sQuery(id+"F2.wireOp",EDGE,"E6.3.104.0"),sQuery(id+"F2.wireOp",EDGE,"E6.2.105.0"),sQuery(id+"F2.wireOp",EDGE,"E6.3.105.0"),sQuery(id+"F2.wireOp",EDGE,"E6.2.106.0"),sQuery(id+"F2.wireOp",EDGE,"E6.3.106.0"),sQuery(id+"F2.wireOp",EDGE,"E6.2.107.0"),sQuery(id+"F2.wireOp",EDGE,"E6.3.107.0"),sQuery(id+"F2.wireOp",EDGE,"E6.2.108.0"),sQuery(id+"F2.wireOp",EDGE,"E6.3.108.0"),sQuery(id+"F2.wireOp",EDGE,"E6.2.109.0"),sQuery(id+"F2.wireOp",EDGE,"E6.3.109.0"),sQuery(id+"F2.wireOp",EDGE,"E6.2.110.0"),sQuery(id+"F2.wireOp",EDGE,"E6.3.110.0"),sQuery(id+"F2.wireOp",EDGE,"E6.2.111.0"),sQuery(id+"F2.wireOp",EDGE,"E6.3.111.0"),sQuery(id+"F2.wireOp",EDGE,"E6.2.112.0"),sQuery(id+"F2.wireOp",EDGE,"E6.3.112.0"),sQuery(id+"F2.wireOp",EDGE,"E6.2.113.0"),sQuery(id+"F2.wireOp",EDGE,"E6.3.113.0"),sQuery(id+"F2.wireOp",EDGE,"E6.2.114.0"),sQuery(id+"F2.wireOp",EDGE,"E6.3.114.0")])],"isStart":true});
            var sketch = newSketch(context, id + "F5", { "sketchPlane" : qUnion([Q0])});
            skLineSegment(sketch, "E7.bottom", {"start": v(2.63, 1.7) * mm, "end": v(-2.63, 1.7) * mm});
            skLineSegment(sketch, "E7.top", {"start": v(2.63, -1.7) * mm, "end": v(-2.63, -1.7) * mm});
            skLineSegment(sketch, "E7.left", {"start": v(2.63, 1.7) * mm, "end": v(2.63, -1.7) * mm});
            skLineSegment(sketch, "E7.right", {"start": v(-2.63, 1.7) * mm, "end": v(-2.63, -1.7) * mm});
            skPoint(sketch, "E7.middle", {"position": v(0, 0) * mm});
            skSolve(sketch);
        }
        {
            var Q0;
            Q0=makeQuery(id+"F5.imprint","IMPRINT",FACE,{"disambiguationData":[TD([[makeQuery(id+"F5.imprint","IMPRINT",EDGE,{"derivedFrom":sQuery(id+"F5.wireOp",EDGE,"E7.bottom")}),1.0]])]});
            extrude(context, id + "F6", {"entities" : qUnion([Q0]), "operationType" : NewBodyOperationType.REMOVE, "oppositeDirection" : true, "depth" : 25 * mm});
        }
        {
            var Q0;
            Q0=makeQuery(id+"F6.boolean.opBoolean","COPY",EDGE,{"derivedFrom":makeQuery(id+"F6.opExtrude","SWEPT_EDGE",EDGE,{"disambiguationData":[OSD([sQuery(id+"F5.wireOp",EDGE,"E7.top"),sQuery(id+"F5.wireOp",EDGE,"E7.right")])]})});
            var Q1;
            Q1=makeQuery(id+"F6.boolean.opBoolean","COPY",EDGE,{"derivedFrom":makeQuery(id+"F6.opExtrude","SWEPT_EDGE",EDGE,{"disambiguationData":[OSD([sQuery(id+"F5.wireOp",EDGE,"E7.bottom"),sQuery(id+"F5.wireOp",EDGE,"E7.left")])]})});
            var Q2;
            Q2=makeQuery(id+"F6.boolean.opBoolean","COPY",EDGE,{"derivedFrom":makeQuery(id+"F6.opExtrude","SWEPT_EDGE",EDGE,{"disambiguationData":[OSD([sQuery(id+"F5.wireOp",EDGE,"E7.bottom"),sQuery(id+"F5.wireOp",EDGE,"E7.right")])]})});
            var Q3;
            Q3=makeQuery(id+"F6.boolean.opBoolean","COPY",EDGE,{"derivedFrom":makeQuery(id+"F6.opExtrude","SWEPT_EDGE",EDGE,{"disambiguationData":[OSD([sQuery(id+"F5.wireOp",EDGE,"E7.top"),sQuery(id+"F5.wireOp",EDGE,"E7.left")])]})});
            fillet(context, id + "F7", {"entities" : qUnion([Q0, Q1, Q2, Q3]), "radius" : 0.5 * mm, "tangentPropagation" : true, "allowEdgeOverflow" : false});
        }
    });
